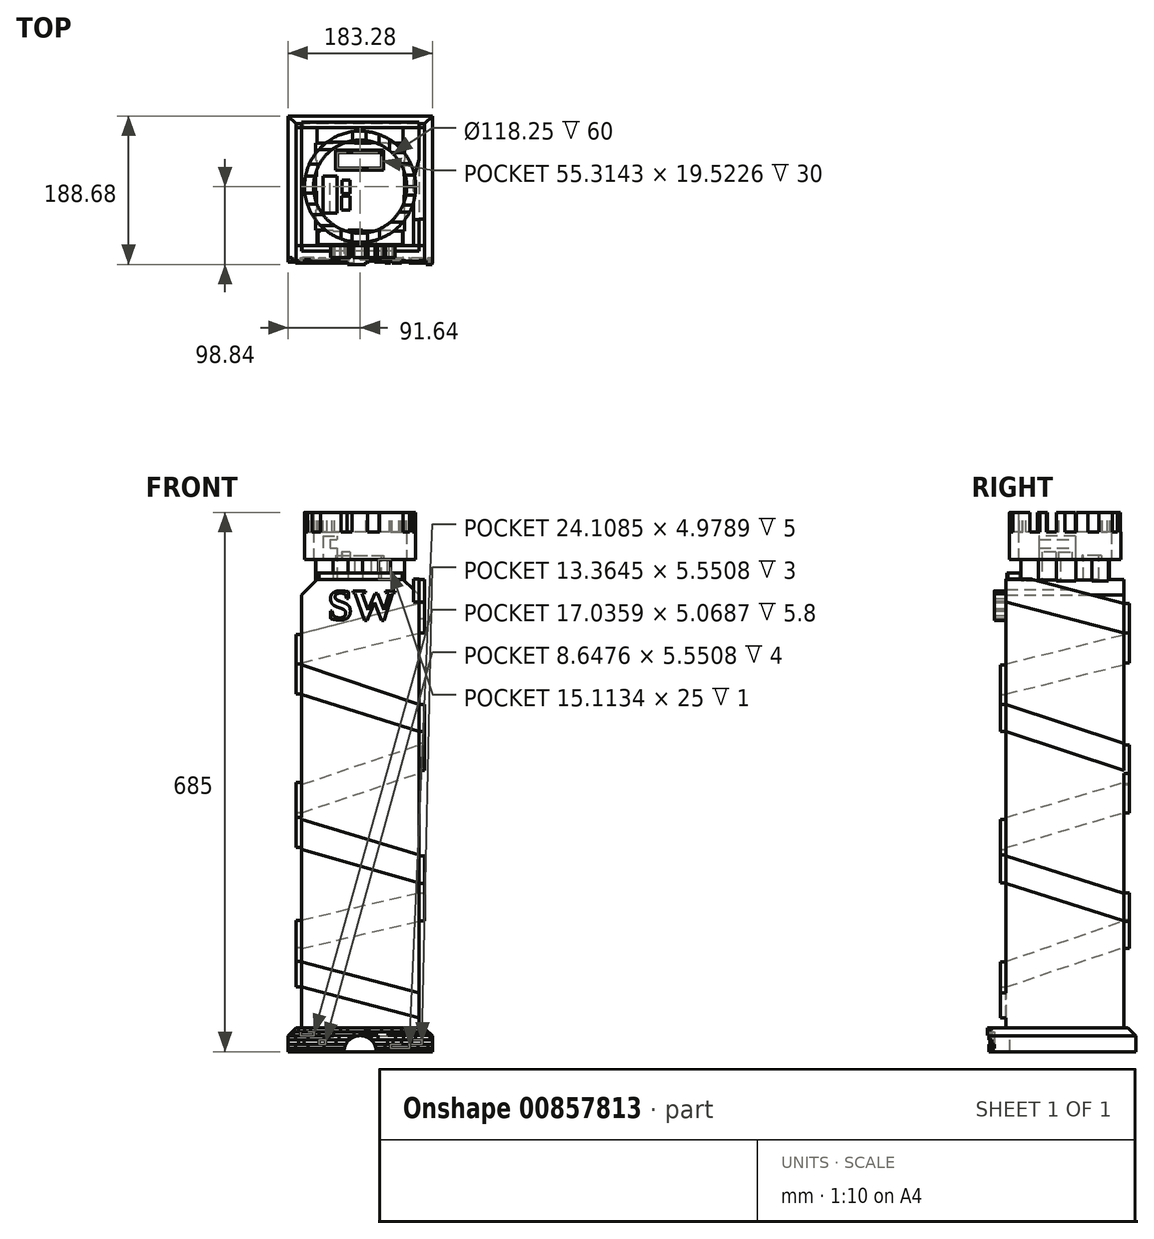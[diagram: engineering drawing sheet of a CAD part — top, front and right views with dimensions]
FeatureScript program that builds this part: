
annotation { "Feature Type Name" : "Feature", "Feature Type Description" : "" }
export const myFeature = defineFeature(function(context is Context, id is Id, definition is map)
    precondition{}
    {
        {
            var Q0;
            Q0=qCreatedBy(makeId("Top.planeOp"),FACE);
            var sketch = newSketch(context, id + "F0", { "sketchPlane" : qUnion([Q0])});
            skLineSegment(sketch, "E0.bottom", {"start": v(-74.68, 74.88) * mm, "end": v(74.68, 74.88) * mm});
            skLineSegment(sketch, "E0.top", {"start": v(-74.68, -74.88) * mm, "end": v(74.68, -74.88) * mm});
            skLineSegment(sketch, "E0.left", {"start": v(-74.68, 74.88) * mm, "end": v(-74.68, -74.88) * mm});
            skLineSegment(sketch, "E0.right", {"start": v(74.68, 74.88) * mm, "end": v(74.68, -74.88) * mm});
            skPoint(sketch, "E0.middle", {"position": v(0, 0) * mm});
            skSolve(sketch);
        }
        {
            var Q0;
            Q0=makeQuery(id+"F0.imprint","IMPRINT",FACE,{"disambiguationData":[TD([[makeQuery(id+"F0.imprint","IMPRINT",EDGE,{"derivedFrom":sQuery(id+"F0.wireOp",EDGE,"E0.bottom")}),-1.0]])]});
            extrude(context, id + "F1", {"entities" : qUnion([Q0]), "depth" : 600 * mm, "offsetDistance" : 25 * mm});
        }
        {
            var Q0;
            Q0=makeQuery(id+"F1.opExtrude","CAP_FACE",FACE,{"disambiguationData":[OSD([sQuery(id+"F0.wireOp",EDGE,"E0.bottom"),sQuery(id+"F0.wireOp",EDGE,"E0.top"),sQuery(id+"F0.wireOp",EDGE,"E0.left"),sQuery(id+"F0.wireOp",EDGE,"E0.right")])],"isStart":true});
            var sketch = newSketch(context, id + "F2", { "sketchPlane" : qUnion([Q0])});
            skLineSegment(sketch, "E1.bottom", {"start": v(-91.64, 89.84) * mm, "end": v(91.64, 89.84) * mm});
            skLineSegment(sketch, "E1.top", {"start": v(-91.64, -89.84) * mm, "end": v(91.64, -89.84) * mm});
            skLineSegment(sketch, "E1.left", {"start": v(-91.64, 89.84) * mm, "end": v(-91.64, -89.84) * mm});
            skLineSegment(sketch, "E1.right", {"start": v(91.64, 89.84) * mm, "end": v(91.64, -89.84) * mm});
            skPoint(sketch, "E1.middle", {"position": v(0, 0) * mm});
            skSolve(sketch);
        }
        {
            var Q0;
            Q0=makeQuery(id+"F1.opExtrude","CAP_FACE",FACE,{"disambiguationData":[OSD([sQuery(id+"F0.wireOp",EDGE,"E0.bottom"),sQuery(id+"F0.wireOp",EDGE,"E0.top"),sQuery(id+"F0.wireOp",EDGE,"E0.left"),sQuery(id+"F0.wireOp",EDGE,"E0.right")])],"isStart":false});
            var sketch = newSketch(context, id + "F3", { "sketchPlane" : qUnion([Q0])});
            skLineSegment(sketch, "E2.bottom", {"start": v(-54.57, 54.23) * mm, "end": v(54.57, 54.23) * mm});
            skLineSegment(sketch, "E2.top", {"start": v(-54.57, -54.23) * mm, "end": v(54.57, -54.23) * mm});
            skLineSegment(sketch, "E2.left", {"start": v(-54.57, 54.23) * mm, "end": v(-54.57, -54.23) * mm});
            skLineSegment(sketch, "E2.right", {"start": v(54.57, 54.23) * mm, "end": v(54.57, -54.23) * mm});
            skPoint(sketch, "E2.middle", {"position": v(0, 0) * mm});
            skSolve(sketch);
        }
        {
            var Q0;
            Q0=makeQuery(id+"F3.imprint","IMPRINT",FACE,{"disambiguationData":[TD([[makeQuery(id+"F3.imprint","IMPRINT",EDGE,{"derivedFrom":sQuery(id+"F3.wireOp",EDGE,"E2.bottom")}),-1.0]])]});
            extrude(context, id + "F4", {"entities" : qUnion([Q0]), "operationType" : NewBodyOperationType.ADD, "depth" : 25 * mm, "offsetDistance" : 25 * mm});
        }
        {
            var Q0;
            Q0=makeQuery(id+"F4.opExtrude","CAP_FACE",FACE,{"disambiguationData":[OSD([sQuery(id+"F3.wireOp",EDGE,"E2.bottom"),sQuery(id+"F3.wireOp",EDGE,"E2.top"),sQuery(id+"F3.wireOp",EDGE,"E2.left"),sQuery(id+"F3.wireOp",EDGE,"E2.right")])],"isStart":false});
            var sketch = newSketch(context, id + "F5", { "sketchPlane" : qUnion([Q0])});
            skCircle(sketch, "E3", {"center": v(0, 0) * mm, "radius": 70.63 * mm});
            skCircle(sketch, "E4", {"center": v(0, 0) * mm, "radius": 59.12 * mm});
            skSolve(sketch);
        }
        {
            var Q0;
            {var subQ0=sQuery(id+"F5.wireOp",EDGE,"E3");var subQ1=makeQuery(id+"F4.opExtrude","CAP_EDGE",EDGE,{"disambiguationData":[OSD([sQuery(id+"F3.wireOp",EDGE,"E2.bottom")])],"isStart":false});var subQ2=makeQuery(id+"F5.imprint","INTERSECT",VERTEX,{"disambiguationData":[OD(0.0)],"derivedFrom":[subQ1,subQ0]});Q0=makeQuery(id+"F5.imprint","IMPRINT",FACE,{"disambiguationData":[TD([[makeQuery(id+"F5.imprint","IMPRINT",EDGE,{"disambiguationData":[TD([[subQ2,-1.0]])],"derivedFrom":subQ0}),1.0]])]});}
            var Q1;
            {var subQ0=sQuery(id+"F5.wireOp",EDGE,"E3");var subQ1=makeQuery(id+"F4.opExtrude","CAP_EDGE",EDGE,{"disambiguationData":[OSD([sQuery(id+"F3.wireOp",EDGE,"E2.bottom")])],"isStart":false});var subQ2=makeQuery(id+"F5.imprint","INTERSECT",VERTEX,{"disambiguationData":[OD(1.0)],"derivedFrom":[subQ1,subQ0]});Q1=makeQuery(id+"F5.imprint","IMPRINT",FACE,{"disambiguationData":[TD([[makeQuery(id+"F5.imprint","IMPRINT",EDGE,{"disambiguationData":[TD([[subQ2,-1.0]])],"derivedFrom":subQ0}),1.0]])]});}
            var Q2;
            {var subQ0=sQuery(id+"F5.wireOp",EDGE,"E3");var subQ1=makeQuery(id+"F4.opExtrude","CAP_EDGE",EDGE,{"disambiguationData":[OSD([sQuery(id+"F3.wireOp",EDGE,"E2.left")])],"isStart":false});var subQ2=makeQuery(id+"F5.imprint","INTERSECT",VERTEX,{"disambiguationData":[OD(0.0)],"derivedFrom":[subQ1,subQ0]});Q2=makeQuery(id+"F5.imprint","IMPRINT",FACE,{"disambiguationData":[TD([[makeQuery(id+"F5.imprint","IMPRINT",EDGE,{"disambiguationData":[TD([[subQ2,-1.0]])],"derivedFrom":subQ0}),1.0]])]});}
            var Q3;
            {var subQ0=sQuery(id+"F5.wireOp",EDGE,"E3");var subQ1=makeQuery(id+"F4.opExtrude","CAP_EDGE",EDGE,{"disambiguationData":[OSD([sQuery(id+"F3.wireOp",EDGE,"E2.top")])],"isStart":false});var subQ2=makeQuery(id+"F5.imprint","INTERSECT",VERTEX,{"disambiguationData":[OD(0.0)],"derivedFrom":[subQ1,subQ0]});Q3=makeQuery(id+"F5.imprint","IMPRINT",FACE,{"disambiguationData":[TD([[makeQuery(id+"F5.imprint","IMPRINT",EDGE,{"disambiguationData":[TD([[subQ2,-1.0]])],"derivedFrom":subQ0}),1.0]])]});}
            var Q4;
            {var subQ0=sQuery(id+"F5.wireOp",EDGE,"E3");var subQ1=makeQuery(id+"F4.opExtrude","CAP_EDGE",EDGE,{"disambiguationData":[OSD([sQuery(id+"F3.wireOp",EDGE,"E2.left")])],"isStart":false});var subQ2=makeQuery(id+"F5.imprint","INTERSECT",VERTEX,{"disambiguationData":[OD(1.0)],"derivedFrom":[subQ1,subQ0]});Q4=makeQuery(id+"F5.imprint","IMPRINT",FACE,{"disambiguationData":[TD([[makeQuery(id+"F5.imprint","IMPRINT",EDGE,{"disambiguationData":[TD([[subQ2,-1.0]])],"derivedFrom":subQ0}),1.0]])]});}
            var Q5;
            {var subQ0=sQuery(id+"F5.wireOp",EDGE,"E3");var subQ1=makeQuery(id+"F4.opExtrude","CAP_EDGE",EDGE,{"disambiguationData":[OSD([sQuery(id+"F3.wireOp",EDGE,"E2.top")])],"isStart":false});var subQ2=makeQuery(id+"F5.imprint","INTERSECT",VERTEX,{"disambiguationData":[OD(1.0)],"derivedFrom":[subQ1,subQ0]});Q5=makeQuery(id+"F5.imprint","IMPRINT",FACE,{"disambiguationData":[TD([[makeQuery(id+"F5.imprint","IMPRINT",EDGE,{"disambiguationData":[TD([[subQ2,-1.0]])],"derivedFrom":subQ0}),1.0]])]});}
            var Q6;
            {var subQ0=sQuery(id+"F5.wireOp",EDGE,"E3");var subQ1=makeQuery(id+"F4.opExtrude","CAP_EDGE",EDGE,{"disambiguationData":[OSD([sQuery(id+"F3.wireOp",EDGE,"E2.right")])],"isStart":false});var subQ2=makeQuery(id+"F5.imprint","INTERSECT",VERTEX,{"disambiguationData":[OD(0.0)],"derivedFrom":[subQ1,subQ0]});Q6=makeQuery(id+"F5.imprint","IMPRINT",FACE,{"disambiguationData":[TD([[makeQuery(id+"F5.imprint","IMPRINT",EDGE,{"disambiguationData":[TD([[subQ2,1.0]])],"derivedFrom":subQ0}),1.0]])]});}
            var Q7;
            {var subQ0=sQuery(id+"F5.wireOp",EDGE,"E3");var subQ1=makeQuery(id+"F4.opExtrude","CAP_EDGE",EDGE,{"disambiguationData":[OSD([sQuery(id+"F3.wireOp",EDGE,"E2.bottom")])],"isStart":false});var subQ2=makeQuery(id+"F5.imprint","INTERSECT",VERTEX,{"disambiguationData":[OD(0.0)],"derivedFrom":[subQ1,subQ0]});Q7=makeQuery(id+"F5.imprint","IMPRINT",FACE,{"disambiguationData":[TD([[makeQuery(id+"F5.imprint","IMPRINT",EDGE,{"disambiguationData":[TD([[subQ2,1.0]])],"derivedFrom":subQ0}),1.0]])]});}
            extrude(context, id + "F6", {"entities" : qUnion([Q0, Q1, Q2, Q3, Q4, Q5, Q6, Q7]), "operationType" : NewBodyOperationType.ADD, "depth" : 60 * mm, "offsetDistance" : 25 * mm});
        }
        {
            var Q0;
            Q0=makeQuery(id+"F6.opExtrude","CAP_FACE",FACE,{"disambiguationData":[OSD([sQuery(id+"F5.wireOp",EDGE,"E3"),sQuery(id+"F5.wireOp",EDGE,"E4")])],"isStart":false});
            var sketch = newSketch(context, id + "F7", { "sketchPlane" : qUnion([Q0])});
            skLineSegment(sketch, "E5.bottom", {"start": v(-9.47, 76.95) * mm, "end": v(7.75, 76.95) * mm});
            skLineSegment(sketch, "E5.top", {"start": v(-9.47, 53.88) * mm, "end": v(7.75, 53.88) * mm});
            skLineSegment(sketch, "E5.left", {"start": v(-9.47, 76.95) * mm, "end": v(-9.47, 53.88) * mm});
            skLineSegment(sketch, "E5.right", {"start": v(7.75, 76.95) * mm, "end": v(7.75, 53.88) * mm});
            skLineSegment(sketch, "E6.bottom", {"start": v(37.36, 69.37) * mm, "end": v(24.27, 69.37) * mm});
            skLineSegment(sketch, "E6.top", {"start": v(37.36, 43.2) * mm, "end": v(24.27, 43.2) * mm});
            skLineSegment(sketch, "E6.left", {"start": v(37.36, 69.37) * mm, "end": v(37.36, 43.2) * mm});
            skLineSegment(sketch, "E6.right", {"start": v(24.27, 69.37) * mm, "end": v(24.27, 43.2) * mm});
            skPoint(sketch, "E7.firstSnap0", {"position": v(30.81, 43.2) * mm});
            skLineSegment(sketch, "E7.bottom", {"start": v(65.59, 43.2) * mm, "end": v(39.77, 43.2) * mm});
            skLineSegment(sketch, "E7.top", {"start": v(65.59, 29.1) * mm, "end": v(39.77, 29.1) * mm});
            skLineSegment(sketch, "E7.left", {"start": v(65.59, 43.2) * mm, "end": v(65.59, 29.1) * mm});
            skLineSegment(sketch, "E7.right", {"start": v(39.77, 43.2) * mm, "end": v(39.77, 29.1) * mm});
            skLineSegment(sketch, "E8.bottom", {"start": v(74.54, 14.63) * mm, "end": v(52.5, 14.63) * mm});
            skLineSegment(sketch, "E8.top", {"start": v(74.54, 0) * mm, "end": v(52.5, 0) * mm});
            skLineSegment(sketch, "E8.left", {"start": v(74.54, 14.63) * mm, "end": v(74.54, 0) * mm});
            skLineSegment(sketch, "E8.right", {"start": v(52.5, 14.63) * mm, "end": v(52.5, 0) * mm});
            skLineSegment(sketch, "E9.bottom", {"start": v(71.44, -23.58) * mm, "end": v(42.86, -23.58) * mm});
            skLineSegment(sketch, "E9.top", {"start": v(71.44, -10.85) * mm, "end": v(42.86, -10.85) * mm});
            skLineSegment(sketch, "E9.left", {"start": v(71.44, -23.58) * mm, "end": v(71.44, -10.85) * mm});
            skLineSegment(sketch, "E9.right", {"start": v(42.86, -23.58) * mm, "end": v(42.86, -10.85) * mm});
            skLineSegment(sketch, "E10.bottom", {"start": v(29.78, -32.2) * mm, "end": v(69.03, -32.2) * mm});
            skLineSegment(sketch, "E10.top", {"start": v(29.78, -44.93) * mm, "end": v(69.03, -44.93) * mm});
            skLineSegment(sketch, "E10.left", {"start": v(29.78, -32.2) * mm, "end": v(29.78, -44.93) * mm});
            skLineSegment(sketch, "E10.right", {"start": v(69.03, -32.2) * mm, "end": v(69.03, -44.93) * mm});
            skLineSegment(sketch, "E11.bottom", {"start": v(9.47, -45.27) * mm, "end": v(24.96, -45.27) * mm});
            skLineSegment(sketch, "E11.top", {"start": v(9.47, -75.23) * mm, "end": v(24.96, -75.23) * mm});
            skLineSegment(sketch, "E11.left", {"start": v(9.47, -45.27) * mm, "end": v(9.47, -75.23) * mm});
            skLineSegment(sketch, "E11.right", {"start": v(24.96, -45.27) * mm, "end": v(24.96, -75.23) * mm});
            skLineSegment(sketch, "E12.bottom", {"start": v(-24.27, -41.14) * mm, "end": v(-10.5, -41.14) * mm});
            skLineSegment(sketch, "E12.top", {"start": v(-24.27, -74.88) * mm, "end": v(-10.5, -74.88) * mm});
            skLineSegment(sketch, "E12.left", {"start": v(-24.27, -41.14) * mm, "end": v(-24.27, -74.88) * mm});
            skLineSegment(sketch, "E12.right", {"start": v(-10.5, -41.14) * mm, "end": v(-10.5, -74.88) * mm});
            skLineSegment(sketch, "E13.bottom", {"start": v(-71.78, -35.29) * mm, "end": v(-32.25, -35.29) * mm});
            skLineSegment(sketch, "E13.top", {"start": v(-71.78, -49.55) * mm, "end": v(-32.25, -49.55) * mm});
            skLineSegment(sketch, "E13.left", {"start": v(-71.78, -35.29) * mm, "end": v(-71.78, -49.55) * mm});
            skLineSegment(sketch, "E13.right", {"start": v(-32.25, -35.29) * mm, "end": v(-32.25, -49.55) * mm});
            skLineSegment(sketch, "E14.bottom", {"start": v(-75.23, -8.1) * mm, "end": v(-46.65, -8.1) * mm});
            skLineSegment(sketch, "E14.top", {"start": v(-75.23, -22.2) * mm, "end": v(-46.65, -22.2) * mm});
            skLineSegment(sketch, "E14.left", {"start": v(-75.23, -8.1) * mm, "end": v(-75.23, -22.2) * mm});
            skLineSegment(sketch, "E14.right", {"start": v(-46.65, -8.1) * mm, "end": v(-46.65, -22.2) * mm});
            skLineSegment(sketch, "E15.bottom", {"start": v(-73.5, 28.4) * mm, "end": v(-47.68, 28.4) * mm});
            skLineSegment(sketch, "E15.top", {"start": v(-73.5, 13.26) * mm, "end": v(-47.68, 13.26) * mm});
            skLineSegment(sketch, "E15.left", {"start": v(-73.5, 28.4) * mm, "end": v(-73.5, 13.26) * mm});
            skLineSegment(sketch, "E15.right", {"start": v(-47.68, 28.4) * mm, "end": v(-47.68, 13.26) * mm});
            skLineSegment(sketch, "E16.bottom", {"start": v(-67.3, 47.34) * mm, "end": v(-16.29, 47.34) * mm});
            skLineSegment(sketch, "E16.top", {"start": v(-67.3, 56.84) * mm, "end": v(-16.29, 56.84) * mm});
            skLineSegment(sketch, "E16.left", {"start": v(-67.3, 47.34) * mm, "end": v(-67.3, 56.84) * mm});
            skLineSegment(sketch, "E16.right", {"start": v(-16.29, 47.34) * mm, "end": v(-16.29, 56.84) * mm});
            skSolve(sketch);
        }
        {
            var Q0;
            {var subQ0=sQuery(id+"F7.wireOp",EDGE,"E6.left");var subQ1=makeQuery(id+"F6.opExtrude","CAP_EDGE",EDGE,{"disambiguationData":[OSD([sQuery(id+"F5.wireOp",EDGE,"E3")])],"isStart":false});var subQ2=makeQuery(id+"F7.imprint","INTERSECT",VERTEX,{"derivedFrom":[subQ1,subQ0]});Q0=makeQuery(id+"F7.imprint","IMPRINT",FACE,{"disambiguationData":[TD([[makeQuery(id+"F7.imprint","IMPRINT",EDGE,{"disambiguationData":[TD([[subQ2,-1.0]])],"derivedFrom":subQ0}),-1.0]])]});}
            var Q1;
            {var subQ0=sQuery(id+"F7.wireOp",EDGE,"E5.left");var subQ1=makeQuery(id+"F6.opExtrude","CAP_EDGE",EDGE,{"disambiguationData":[OSD([sQuery(id+"F5.wireOp",EDGE,"E3")])],"isStart":false});var subQ2=makeQuery(id+"F7.imprint","INTERSECT",VERTEX,{"derivedFrom":[subQ1,subQ0]});Q1=makeQuery(id+"F7.imprint","IMPRINT",FACE,{"disambiguationData":[TD([[makeQuery(id+"F7.imprint","IMPRINT",EDGE,{"disambiguationData":[TD([[subQ2,-1.0]])],"derivedFrom":subQ0}),1.0]])]});}
            var Q2;
            {var subQ0=sQuery(id+"F7.wireOp",EDGE,"E16.bottom");var subQ1=makeQuery(id+"F6.opExtrude","CAP_EDGE",EDGE,{"disambiguationData":[OSD([sQuery(id+"F5.wireOp",EDGE,"E3")])],"isStart":false});var subQ2=makeQuery(id+"F7.imprint","INTERSECT",VERTEX,{"derivedFrom":[subQ1,subQ0]});Q2=makeQuery(id+"F7.imprint","IMPRINT",FACE,{"disambiguationData":[TD([[makeQuery(id+"F7.imprint","IMPRINT",EDGE,{"disambiguationData":[TD([[subQ2,-1.0]])],"derivedFrom":subQ0}),1.0]])]});}
            var Q3;
            {var subQ0=sQuery(id+"F7.wireOp",EDGE,"E15.bottom");var subQ1=makeQuery(id+"F6.opExtrude","CAP_EDGE",EDGE,{"disambiguationData":[OSD([sQuery(id+"F5.wireOp",EDGE,"E3")])],"isStart":false});var subQ2=makeQuery(id+"F7.imprint","INTERSECT",VERTEX,{"derivedFrom":[subQ1,subQ0]});Q3=makeQuery(id+"F7.imprint","IMPRINT",FACE,{"disambiguationData":[TD([[makeQuery(id+"F7.imprint","IMPRINT",EDGE,{"disambiguationData":[TD([[subQ2,-1.0]])],"derivedFrom":subQ0}),-1.0]])]});}
            var Q4;
            {var subQ0=sQuery(id+"F7.wireOp",EDGE,"E14.bottom");var subQ1=makeQuery(id+"F6.opExtrude","CAP_EDGE",EDGE,{"disambiguationData":[OSD([sQuery(id+"F5.wireOp",EDGE,"E3")])],"isStart":false});var subQ2=makeQuery(id+"F7.imprint","INTERSECT",VERTEX,{"derivedFrom":[subQ1,subQ0]});Q4=makeQuery(id+"F7.imprint","IMPRINT",FACE,{"disambiguationData":[TD([[makeQuery(id+"F7.imprint","IMPRINT",EDGE,{"disambiguationData":[TD([[subQ2,-1.0]])],"derivedFrom":subQ0}),-1.0]])]});}
            var Q5;
            {var subQ0=sQuery(id+"F7.wireOp",EDGE,"E13.bottom");var subQ1=makeQuery(id+"F6.opExtrude","CAP_EDGE",EDGE,{"disambiguationData":[OSD([sQuery(id+"F5.wireOp",EDGE,"E3")])],"isStart":false});var subQ2=makeQuery(id+"F7.imprint","INTERSECT",VERTEX,{"derivedFrom":[subQ1,subQ0]});Q5=makeQuery(id+"F7.imprint","IMPRINT",FACE,{"disambiguationData":[TD([[makeQuery(id+"F7.imprint","IMPRINT",EDGE,{"disambiguationData":[TD([[subQ2,-1.0]])],"derivedFrom":subQ0}),-1.0]])]});}
            var Q6;
            {var subQ0=sQuery(id+"F7.wireOp",EDGE,"E12.left");var subQ1=makeQuery(id+"F6.opExtrude","CAP_EDGE",EDGE,{"disambiguationData":[OSD([sQuery(id+"F5.wireOp",EDGE,"E3")])],"isStart":false});var subQ2=makeQuery(id+"F7.imprint","INTERSECT",VERTEX,{"derivedFrom":[subQ1,subQ0]});Q6=makeQuery(id+"F7.imprint","IMPRINT",FACE,{"disambiguationData":[TD([[makeQuery(id+"F7.imprint","IMPRINT",EDGE,{"disambiguationData":[TD([[subQ2,1.0]])],"derivedFrom":subQ0}),1.0]])]});}
            var Q7;
            {var subQ0=sQuery(id+"F7.wireOp",EDGE,"E11.left");var subQ1=makeQuery(id+"F6.opExtrude","CAP_EDGE",EDGE,{"disambiguationData":[OSD([sQuery(id+"F5.wireOp",EDGE,"E3")])],"isStart":false});var subQ2=makeQuery(id+"F7.imprint","INTERSECT",VERTEX,{"derivedFrom":[subQ1,subQ0]});Q7=makeQuery(id+"F7.imprint","IMPRINT",FACE,{"disambiguationData":[TD([[makeQuery(id+"F7.imprint","IMPRINT",EDGE,{"disambiguationData":[TD([[subQ2,1.0]])],"derivedFrom":subQ0}),1.0]])]});}
            var Q8;
            {var subQ0=sQuery(id+"F7.wireOp",EDGE,"E10.bottom");var subQ1=makeQuery(id+"F6.opExtrude","CAP_EDGE",EDGE,{"disambiguationData":[OSD([sQuery(id+"F5.wireOp",EDGE,"E3")])],"isStart":false});var subQ2=makeQuery(id+"F7.imprint","INTERSECT",VERTEX,{"derivedFrom":[subQ1,subQ0]});Q8=makeQuery(id+"F7.imprint","IMPRINT",FACE,{"disambiguationData":[TD([[makeQuery(id+"F7.imprint","IMPRINT",EDGE,{"disambiguationData":[TD([[subQ2,1.0]])],"derivedFrom":subQ0}),-1.0]])]});}
            var Q9;
            {var subQ0=sQuery(id+"F7.wireOp",EDGE,"E9.bottom");var subQ1=makeQuery(id+"F6.opExtrude","CAP_EDGE",EDGE,{"disambiguationData":[OSD([sQuery(id+"F5.wireOp",EDGE,"E3")])],"isStart":false});var subQ2=makeQuery(id+"F7.imprint","INTERSECT",VERTEX,{"derivedFrom":[subQ1,subQ0]});Q9=makeQuery(id+"F7.imprint","IMPRINT",FACE,{"disambiguationData":[TD([[makeQuery(id+"F7.imprint","IMPRINT",EDGE,{"disambiguationData":[TD([[subQ2,-1.0]])],"derivedFrom":subQ0}),-1.0]])]});}
            var Q10;
            {var subQ0=sQuery(id+"F7.wireOp",EDGE,"E8.bottom");var subQ1=makeQuery(id+"F6.opExtrude","CAP_EDGE",EDGE,{"disambiguationData":[OSD([sQuery(id+"F5.wireOp",EDGE,"E3")])],"isStart":false});var subQ2=makeQuery(id+"F7.imprint","INTERSECT",VERTEX,{"derivedFrom":[subQ1,subQ0]});Q10=makeQuery(id+"F7.imprint","IMPRINT",FACE,{"disambiguationData":[TD([[makeQuery(id+"F7.imprint","IMPRINT",EDGE,{"disambiguationData":[TD([[subQ2,-1.0]])],"derivedFrom":subQ0}),1.0]])]});}
            var Q11;
            {var subQ0=sQuery(id+"F7.wireOp",EDGE,"E7.bottom");var subQ1=makeQuery(id+"F6.opExtrude","CAP_EDGE",EDGE,{"disambiguationData":[OSD([sQuery(id+"F5.wireOp",EDGE,"E3")])],"isStart":false});var subQ2=makeQuery(id+"F7.imprint","INTERSECT",VERTEX,{"derivedFrom":[subQ1,subQ0]});Q11=makeQuery(id+"F7.imprint","IMPRINT",FACE,{"disambiguationData":[TD([[makeQuery(id+"F7.imprint","IMPRINT",EDGE,{"disambiguationData":[TD([[subQ2,-1.0]])],"derivedFrom":subQ0}),1.0]])]});}
            extrude(context, id + "F8", {"entities" : qUnion([Q0, Q1, Q2, Q3, Q4, Q5, Q6, Q7, Q8, Q9, Q10, Q11]), "operationType" : NewBodyOperationType.REMOVE, "oppositeDirection" : true, "depth" : 25 * mm, "offsetDistance" : 25 * mm});
        }
        {
            var Q0;
            Q0=makeQuery(id+"F2.imprint","IMPRINT",FACE,{"disambiguationData":[TD([[makeQuery(id+"F2.imprint","IMPRINT",EDGE,{"derivedFrom":sQuery(id+"F2.wireOp",EDGE,"E1.bottom")}),-1.0]])]});
            extrude(context, id + "F9", {"entities" : qUnion([Q0]), "operationType" : NewBodyOperationType.ADD, "oppositeDirection" : true, "depth" : 30 * mm, "offsetDistance" : 25 * mm});
        }
        {
            var Q0;
            Q0=makeQuery(id+"F1.opExtrude","SWEPT_FACE",FACE,{"disambiguationData":[OSD([sQuery(id+"F0.wireOp",EDGE,"E0.top")])]});
            var sketch = newSketch(context, id + "F10", { "sketchPlane" : qUnion([Q0])});
            skLineSegment(sketch, "E17", {"start": v(74.68, 42.98) * mm, "end": v(-74.68, 82.43) * mm});
            skLineSegment(sketch, "E18", {"start": v(74.68, 74.92) * mm, "end": v(-74.68, 114.36) * mm});
            skSolve(sketch);
        }
        {
            var Q0;
            Q0=makeQuery(id+"F1.opExtrude","SWEPT_FACE",FACE,{"disambiguationData":[OSD([sQuery(id+"F0.wireOp",EDGE,"E0.left")])]});
            var sketch = newSketch(context, id + "F11", { "sketchPlane" : qUnion([Q0])});
            skLineSegment(sketch, "E19", {"start": v(74.88, 114.53) * mm, "end": v(-74.88, 166.66) * mm});
            skLineSegment(sketch, "E20", {"start": v(74.88, 82.26) * mm, "end": v(-74.88, 132.53) * mm});
            skSolve(sketch);
        }
        {
            var Q0;
            Q0=makeQuery(id+"F1.opExtrude","SWEPT_FACE",FACE,{"disambiguationData":[OSD([sQuery(id+"F0.wireOp",EDGE,"E0.bottom")])]});
            var sketch = newSketch(context, id + "F12", { "sketchPlane" : qUnion([Q0])});
            skLineSegment(sketch, "E21", {"start": v(74.68, 167.39) * mm, "end": v(-74.68, 201.82) * mm});
            skLineSegment(sketch, "E22", {"start": v(74.68, 131.22) * mm, "end": v(-74.68, 165.65) * mm});
            skSolve(sketch);
        }
        {
            var Q0;
            Q0=makeQuery(id+"F1.opExtrude","SWEPT_FACE",FACE,{"disambiguationData":[OSD([sQuery(id+"F0.wireOp",EDGE,"E0.right")])]});
            var sketch = newSketch(context, id + "F13", { "sketchPlane" : qUnion([Q0])});
            skLineSegment(sketch, "E23", {"start": v(74.88, 200.88) * mm, "end": v(-74.88, 248.94) * mm});
            skLineSegment(sketch, "E24", {"start": v(74.88, 165.93) * mm, "end": v(-74.88, 213.99) * mm});
            skSolve(sketch);
        }
        {
            var Q0;
            {var subQ0=sQuery(id+"F10.wireOp",EDGE,"E18");Q0=makeQuery(id+"F10.imprint","IMPRINT",FACE,{"disambiguationData":[TD([[makeQuery(id+"F10.imprint","IMPRINT",EDGE,{"derivedFrom":subQ0}),-1.0]])]});}
            var sketch = newSketch(context, id + "F14", { "sketchPlane" : qUnion([Q0])});
            skLineSegment(sketch, "E25", {"start": v(74.9, 249.82) * mm, "end": v(-76.45, 295.53) * mm});
            skLineSegment(sketch, "E26", {"start": v(76.45, 213.99) * mm, "end": v(-76.45, 257.67) * mm});
            skSolve(sketch);
        }
        {
            var Q0;
            {var subQ0=sQuery(id+"F11.wireOp",EDGE,"E19");Q0=makeQuery(id+"F11.imprint","IMPRINT",FACE,{"disambiguationData":[TD([[makeQuery(id+"F11.imprint","IMPRINT",EDGE,{"derivedFrom":subQ0}),-1.0]])]});}
            var sketch = newSketch(context, id + "F15", { "sketchPlane" : qUnion([Q0])});
            skLineSegment(sketch, "E27", {"start": v(76.45, 297) * mm, "end": v(-75, 342.13) * mm});
            skLineSegment(sketch, "E28", {"start": v(75, 259.13) * mm, "end": v(-75, 303.84) * mm});
            skSolve(sketch);
        }
        {
            var Q0;
            {var subQ0=sQuery(id+"F12.wireOp",EDGE,"E21");Q0=makeQuery(id+"F12.imprint","IMPRINT",FACE,{"disambiguationData":[TD([[makeQuery(id+"F12.imprint","IMPRINT",EDGE,{"derivedFrom":subQ0}),-1.0]])]});}
            var sketch = newSketch(context, id + "F16", { "sketchPlane" : qUnion([Q0])});
            skLineSegment(sketch, "E29", {"start": v(72.56, 340.05) * mm, "end": v(-76.45, 390.19) * mm});
            skLineSegment(sketch, "E30", {"start": v(76.45, 302.82) * mm, "end": v(-76.45, 354.26) * mm});
            skLineSegment(sketch, "E31", {"start": v(72.56, 340.05) * mm, "end": v(74.65, 339.46) * mm});
            skLineSegment(sketch, "E32", {"start": v(-76.45, 390.19) * mm, "end": v(-76.45, 354.26) * mm});
            skLineSegment(sketch, "E33", {"start": v(74.65, 339.46) * mm, "end": v(76.45, 302.82) * mm});
            skSolve(sketch);
        }
        {
            var Q0;
            {var subQ0=sQuery(id+"F13.wireOp",EDGE,"E23");Q0=makeQuery(id+"F13.imprint","IMPRINT",FACE,{"disambiguationData":[TD([[makeQuery(id+"F13.imprint","IMPRINT",EDGE,{"derivedFrom":subQ0}),-1.0]])]});}
            var sketch = newSketch(context, id + "F17", { "sketchPlane" : qUnion([Q0])});
            skLineSegment(sketch, "E34", {"start": v(75, 391.64) * mm, "end": v(-75, 441.16) * mm});
            skLineSegment(sketch, "E35", {"start": v(76.45, 356.7) * mm, "end": v(-75, 406.69) * mm});
            skSolve(sketch);
        }
        {
            var Q0;
            {var subQ0=sQuery(id+"F10.wireOp",EDGE,"E18");Q0=makeQuery(id+"F10.imprint","IMPRINT",FACE,{"disambiguationData":[TD([[makeQuery(id+"F10.imprint","IMPRINT",EDGE,{"derivedFrom":subQ0}),-1.0]])]});}
            var sketch = newSketch(context, id + "F18", { "sketchPlane" : qUnion([Q0])});
            skLineSegment(sketch, "E36", {"start": v(75.9, 440.45) * mm, "end": v(-73.68, 491.16) * mm});
            skLineSegment(sketch, "E37", {"start": v(74.17, 406.95) * mm, "end": v(-73.68, 453.3) * mm});
            skLineSegment(sketch, "E38", {"start": v(74.17, 406.95) * mm, "end": v(74.72, 406.78) * mm});
            skLineSegment(sketch, "E39", {"start": v(-73.68, 453.3) * mm, "end": v(-74.71, 453.62) * mm});
            skLineSegment(sketch, "E40", {"start": v(-73.68, 491.16) * mm, "end": v(-74.71, 491.48) * mm});
            skSolve(sketch);
        }
        {
            var Q0;
            {var subQ1=sQuery(id+"F0.wireOp",EDGE,"E0.left");var subQ3=makeQuery(id+"F1.opExtrude","CAP_EDGE",EDGE,{"disambiguationData":[OSD([subQ1])],"isStart":false});var subQ10=makeQuery(id+"F11.imprint","IMPRINT",EDGE,{"derivedFrom":subQ3});Q0=makeQuery(id+"F15.imprint","IMPRINT",FACE,{"disambiguationData":[TD([[makeQuery(id+"F15.imprint","IMPRINT",EDGE,{"derivedFrom":subQ10}),-1.0]])]});}
            var sketch = newSketch(context, id + "F19", { "sketchPlane" : qUnion([Q0])});
            skLineSegment(sketch, "E41", {"start": v(76.45, 492.12) * mm, "end": v(-75, 529.98) * mm});
            skLineSegment(sketch, "E42", {"start": v(75, 454.26) * mm, "end": v(-75, 491.76) * mm});
            skSolve(sketch);
        }
        {
            var Q0;
            {var subQ1=sQuery(id+"F0.wireOp",EDGE,"E0.bottom");var subQ3=makeQuery(id+"F1.opExtrude","CAP_EDGE",EDGE,{"disambiguationData":[OSD([subQ1])],"isStart":false});var subQ10=makeQuery(id+"F12.imprint","IMPRINT",EDGE,{"derivedFrom":subQ3});Q0=makeQuery(id+"F16.imprint","IMPRINT",FACE,{"disambiguationData":[TD([[makeQuery(id+"F16.imprint","IMPRINT",EDGE,{"derivedFrom":subQ10}),1.0]])]});}
            var sketch = newSketch(context, id + "F20", { "sketchPlane" : qUnion([Q0])});
            skLineSegment(sketch, "E43", {"start": v(73.54, 531.44) * mm, "end": v(-75, 569.3) * mm});
            skLineSegment(sketch, "E44", {"start": v(75, 493.58) * mm, "end": v(-75, 531.81) * mm});
            skLineSegment(sketch, "E45", {"start": v(73.54, 531.44) * mm, "end": v(74.7, 531.14) * mm});
            skSolve(sketch);
        }
        {
            var Q0;
            {var subQ1=sQuery(id+"F0.wireOp",EDGE,"E0.right");var subQ3=makeQuery(id+"F1.opExtrude","CAP_EDGE",EDGE,{"disambiguationData":[OSD([subQ1])],"isStart":false});var subQ10=makeQuery(id+"F13.imprint","IMPRINT",EDGE,{"derivedFrom":subQ3});Q0=makeQuery(id+"F17.imprint","IMPRINT",FACE,{"disambiguationData":[TD([[makeQuery(id+"F17.imprint","IMPRINT",EDGE,{"derivedFrom":subQ10}),1.0]])]});}
            var sketch = newSketch(context, id + "F21", { "sketchPlane" : qUnion([Q0])});
            skLineSegment(sketch, "E46", {"start": v(75.08, 569.22) * mm, "end": v(-42.03, 600.15) * mm});
            skLineSegment(sketch, "E47", {"start": v(74.7, 531.71) * mm, "end": v(-74.94, 571.23) * mm});
            skLineSegment(sketch, "E48", {"start": v(-74.94, 571.23) * mm, "end": v(-74.94, 600.15) * mm});
            skLineSegment(sketch, "E49", {"start": v(-74.94, 600.15) * mm, "end": v(-42.03, 600.15) * mm});
            skLineSegment(sketch, "E50", {"start": v(75.08, 569.22) * mm, "end": v(74.7, 531.71) * mm});
            skSolve(sketch);
        }
        {
            var Q0;
            {var subQ0=sQuery(id+"F11.wireOp",EDGE,"E19");Q0=makeQuery(id+"F11.imprint","IMPRINT",FACE,{"disambiguationData":[TD([[makeQuery(id+"F11.imprint","IMPRINT",EDGE,{"derivedFrom":subQ0}),1.0]])]});}
            var Q1;
            Q1 = qSketchRegion(id + "F21", true);
            extrude(context, id + "F22", {"entities" : qUnion([Q0, Q1]), "operationType" : NewBodyOperationType.ADD, "depth" : 7 * mm, "offsetDistance" : 25 * mm});
        }
        {
            var Q0;
            {var subQ0=sQuery(id+"F10.wireOp",EDGE,"E17");Q0=makeQuery(id+"F10.imprint","IMPRINT",FACE,{"disambiguationData":[TD([[makeQuery(id+"F10.imprint","IMPRINT",EDGE,{"derivedFrom":subQ0}),-1.0]])]});}
            extrude(context, id + "F23", {"entities" : qUnion([Q0]), "operationType" : NewBodyOperationType.ADD, "depth" : 7 * mm, "offsetDistance" : 25 * mm});
        }
        {
            var Q0;
            {var subQ0=sQuery(id+"F12.wireOp",EDGE,"E21");Q0=makeQuery(id+"F12.imprint","IMPRINT",FACE,{"disambiguationData":[TD([[makeQuery(id+"F12.imprint","IMPRINT",EDGE,{"derivedFrom":subQ0}),1.0]])]});}
            extrude(context, id + "F24", {"entities" : qUnion([Q0]), "operationType" : NewBodyOperationType.ADD, "depth" : 7 * mm, "offsetDistance" : 25 * mm});
        }
        {
            var Q0;
            {var subQ0=sQuery(id+"F13.wireOp",EDGE,"E23");Q0=makeQuery(id+"F13.imprint","IMPRINT",FACE,{"disambiguationData":[TD([[makeQuery(id+"F13.imprint","IMPRINT",EDGE,{"derivedFrom":subQ0}),1.0]])]});}
            extrude(context, id + "F25", {"entities" : qUnion([Q0]), "operationType" : NewBodyOperationType.ADD, "depth" : 7 * mm, "offsetDistance" : 25 * mm});
        }
        {
            var Q0;
            {var subQ0=sQuery(id+"F14.wireOp",EDGE,"E25");var subQ1=sQuery(id+"F0.wireOp",EDGE,"E0.top");var subQ2=makeQuery(id+"F1.opExtrude","SWEPT_EDGE",EDGE,{"disambiguationData":[OSD([subQ1,sQuery(id+"F0.wireOp",EDGE,"E0.left")])]});var subQ3=makeQuery(id+"F1.opExtrude","CAP_EDGE",EDGE,{"disambiguationData":[OSD([subQ1])],"isStart":false});var subQ5=makeQuery(id+"F10.imprint","IMPRINT",EDGE,{"disambiguationData":[TD([[makeQuery(id+"F10.imprint","INTERSECT",VERTEX,{"derivedFrom":[subQ3,subQ2]}),-1.0]])],"derivedFrom":subQ2});var subQ6=makeQuery(id+"F14.imprint","INTERSECT",VERTEX,{"derivedFrom":[subQ5,subQ0]});Q0=makeQuery(id+"F14.imprint","IMPRINT",FACE,{"disambiguationData":[TD([[makeQuery(id+"F14.imprint","IMPRINT",EDGE,{"disambiguationData":[TD([[subQ6,1.0]])],"derivedFrom":subQ0}),1.0]])]});}
            extrude(context, id + "F26", {"entities" : qUnion([Q0]), "operationType" : NewBodyOperationType.ADD, "depth" : 7 * mm, "offsetDistance" : 25 * mm});
        }
        {
            var Q0;
            {var subQ0=sQuery(id+"F15.wireOp",EDGE,"E27");var subQ1=sQuery(id+"F0.wireOp",EDGE,"E0.left");var subQ2=makeQuery(id+"F1.opExtrude","SWEPT_EDGE",EDGE,{"disambiguationData":[OSD([sQuery(id+"F0.wireOp",EDGE,"E0.bottom"),subQ1])]});var subQ3=makeQuery(id+"F1.opExtrude","CAP_EDGE",EDGE,{"disambiguationData":[OSD([subQ1])],"isStart":false});var subQ5=makeQuery(id+"F11.imprint","IMPRINT",EDGE,{"disambiguationData":[TD([[makeQuery(id+"F11.imprint","INTERSECT",VERTEX,{"derivedFrom":[subQ3,subQ2]}),-1.0]])],"derivedFrom":subQ2});var subQ6=makeQuery(id+"F15.imprint","INTERSECT",VERTEX,{"derivedFrom":[subQ5,subQ0]});Q0=makeQuery(id+"F15.imprint","IMPRINT",FACE,{"disambiguationData":[TD([[makeQuery(id+"F15.imprint","IMPRINT",EDGE,{"disambiguationData":[TD([[subQ6,1.0]])],"derivedFrom":subQ0}),1.0]])]});}
            extrude(context, id + "F27", {"entities" : qUnion([Q0]), "operationType" : NewBodyOperationType.ADD, "depth" : 7 * mm, "offsetDistance" : 25 * mm});
        }
        {
            var Q0;
            {var subQ1=sQuery(id+"F16.wireOp",EDGE,"E31");Q0=makeQuery(id+"F16.imprint","IMPRINT",FACE,{"disambiguationData":[TD([[makeQuery(id+"F16.imprint","IMPRINT",EDGE,{"derivedFrom":subQ1}),-1.0]])]});}
            extrude(context, id + "F28", {"entities" : qUnion([Q0]), "operationType" : NewBodyOperationType.ADD, "depth" : 7 * mm, "offsetDistance" : 25 * mm});
        }
        {
            var Q0;
            {var subQ0=sQuery(id+"F17.wireOp",EDGE,"E34");var subQ1=sQuery(id+"F0.wireOp",EDGE,"E0.right");var subQ2=makeQuery(id+"F1.opExtrude","SWEPT_EDGE",EDGE,{"disambiguationData":[OSD([sQuery(id+"F0.wireOp",EDGE,"E0.bottom"),subQ1])]});var subQ3=makeQuery(id+"F1.opExtrude","CAP_EDGE",EDGE,{"disambiguationData":[OSD([subQ1])],"isStart":false});var subQ5=makeQuery(id+"F13.imprint","IMPRINT",EDGE,{"disambiguationData":[TD([[makeQuery(id+"F13.imprint","INTERSECT",VERTEX,{"derivedFrom":[subQ3,subQ2]}),-1.0]])],"derivedFrom":subQ2});var subQ6=makeQuery(id+"F17.imprint","INTERSECT",VERTEX,{"derivedFrom":[subQ5,subQ0]});Q0=makeQuery(id+"F17.imprint","IMPRINT",FACE,{"disambiguationData":[TD([[makeQuery(id+"F17.imprint","IMPRINT",EDGE,{"disambiguationData":[TD([[subQ6,-1.0]])],"derivedFrom":subQ0}),1.0]])]});}
            extrude(context, id + "F29", {"entities" : qUnion([Q0]), "operationType" : NewBodyOperationType.ADD, "depth" : 7 * mm, "offsetDistance" : 25 * mm});
        }
        {
            var Q0;
            {var subQ1=sQuery(id+"F18.wireOp",EDGE,"E37");Q0=makeQuery(id+"F18.imprint","IMPRINT",FACE,{"disambiguationData":[TD([[makeQuery(id+"F18.imprint","IMPRINT",EDGE,{"derivedFrom":subQ1}),-1.0]])]});}
            extrude(context, id + "F30", {"entities" : qUnion([Q0]), "operationType" : NewBodyOperationType.ADD, "depth" : 7 * mm, "offsetDistance" : 25 * mm});
        }
        {
            var Q0;
            {var subQ0=sQuery(id+"F19.wireOp",EDGE,"E41");var subQ1=sQuery(id+"F0.wireOp",EDGE,"E0.left");var subQ2=makeQuery(id+"F1.opExtrude","SWEPT_EDGE",EDGE,{"disambiguationData":[OSD([sQuery(id+"F0.wireOp",EDGE,"E0.bottom"),subQ1])]});var subQ3=makeQuery(id+"F1.opExtrude","CAP_EDGE",EDGE,{"disambiguationData":[OSD([subQ1])],"isStart":false});var subQ5=makeQuery(id+"F11.imprint","IMPRINT",EDGE,{"disambiguationData":[TD([[makeQuery(id+"F11.imprint","INTERSECT",VERTEX,{"derivedFrom":[subQ3,subQ2]}),-1.0]])],"derivedFrom":subQ2});var subQ6=makeQuery(id+"F11.imprint","IMPRINT",EDGE,{"derivedFrom":subQ3});var subQ8=makeQuery(id+"F15.imprint","IMPRINT",EDGE,{"disambiguationData":[TD([[makeQuery(id+"F15.imprint","INTERSECT",VERTEX,{"derivedFrom":[subQ6,subQ5]}),-1.0]])],"derivedFrom":subQ5});var subQ9=makeQuery(id+"F19.imprint","INTERSECT",VERTEX,{"derivedFrom":[subQ8,subQ0]});Q0=makeQuery(id+"F19.imprint","IMPRINT",FACE,{"disambiguationData":[TD([[makeQuery(id+"F19.imprint","IMPRINT",EDGE,{"disambiguationData":[TD([[subQ9,1.0]])],"derivedFrom":subQ0}),1.0]])]});}
            extrude(context, id + "F31", {"entities" : qUnion([Q0]), "operationType" : NewBodyOperationType.ADD, "depth" : 7 * mm, "offsetDistance" : 25 * mm});
        }
        {
            var Q0;
            {var subQ0=sQuery(id+"F20.wireOp",EDGE,"E45");var subQ11=sQuery(id+"F20.wireOp",EDGE,"E43");var subQ12=makeQuery(id+"F20.imprint","INTERSECT",VERTEX,{"derivedFrom":[subQ11,subQ0]});Q0=makeQuery(id+"F20.imprint","IMPRINT",FACE,{"disambiguationData":[TD([[makeQuery(id+"F20.imprint","IMPRINT",EDGE,{"disambiguationData":[TD([[subQ12,-1.0]])],"derivedFrom":subQ11}),1.0]])]});}
            extrude(context, id + "F32", {"entities" : qUnion([Q0]), "operationType" : NewBodyOperationType.ADD, "depth" : 7 * mm, "offsetDistance" : 25 * mm});
        }
        {
            var Q0;
            {var subQ3=sQuery(id+"F0.wireOp",EDGE,"E0.right");var subQ5=makeQuery(id+"F1.opExtrude","CAP_EDGE",EDGE,{"disambiguationData":[OSD([subQ3])],"isStart":false});var subQ8=makeQuery(id+"F13.imprint","IMPRINT",EDGE,{"derivedFrom":subQ5});var subQ16=sQuery(id+"F21.wireOp",EDGE,"E46");var subQ18=makeQuery(id+"F17.imprint","IMPRINT",EDGE,{"derivedFrom":subQ8});var subQ20=makeQuery(id+"F21.imprint","INTERSECT",VERTEX,{"derivedFrom":[subQ18,subQ16]});Q0=makeQuery(id+"F21.imprint","IMPRINT",FACE,{"disambiguationData":[TD([[makeQuery(id+"F21.imprint","IMPRINT",EDGE,{"disambiguationData":[TD([[subQ20,1.0]])],"derivedFrom":subQ16}),1.0]])]});}
            extrude(context, id + "F33", {"entities" : qUnion([Q0]), "operationType" : NewBodyOperationType.ADD, "depth" : 7 * mm, "offsetDistance" : 25 * mm});
        }
        {
            var Q0;
            Q0=makeQuery(id+"F9.opExtrude","SWEPT_FACE",FACE,{"disambiguationData":[OSD([sQuery(id+"F2.wireOp",EDGE,"E1.bottom")])]});
            var sketch = newSketch(context, id + "F34", { "sketchPlane" : qUnion([Q0])});
            skCircle(sketch, "E51", {"center": v(0, 0) * mm, "radius": 20.4 * mm});
            skSolve(sketch);
        }
        {
            var Q0;
            {var subQ0=sQuery(id+"F34.wireOp",EDGE,"E51");var subQ1=makeQuery(id+"F9.opExtrude","CAP_EDGE",EDGE,{"disambiguationData":[OSD([sQuery(id+"F2.wireOp",EDGE,"E1.bottom")])],"isStart":true});var subQ2=makeQuery(id+"F34.imprint","INTERSECT",VERTEX,{"disambiguationData":[OD(0.0)],"derivedFrom":[subQ1,subQ0]});Q0=makeQuery(id+"F34.imprint","IMPRINT",FACE,{"disambiguationData":[TD([[makeQuery(id+"F34.imprint","IMPRINT",EDGE,{"disambiguationData":[TD([[subQ2,1.0]])],"derivedFrom":subQ0}),1.0]])]});}
            extrude(context, id + "F35", {"entities" : qUnion([Q0]), "operationType" : NewBodyOperationType.REMOVE, "oppositeDirection" : true, "depth" : 20 * mm, "offsetDistance" : 25 * mm});
        }
        {
            var Q0;
            Q0=makeQuery(id+"F9.opExtrude","SWEPT_FACE",FACE,{"disambiguationData":[OSD([sQuery(id+"F2.wireOp",EDGE,"E1.bottom")])]});
            var sketch = newSketch(context, id + "F36", { "sketchPlane" : qUnion([Q0])});
            skLineSegment(sketch, "E52", {"start": v(-91.64, 25.43) * mm, "end": v(91.64, 25.43) * mm});
            skLineSegment(sketch, "E53", {"start": v(91.64, 20.46) * mm, "end": v(-91.64, 20.36) * mm});
            skLineSegment(sketch, "E54", {"start": v(-91.64, 20.36) * mm, "end": v(-91.64, 15) * mm});
            skLineSegment(sketch, "E55", {"start": v(-91.64, 15) * mm, "end": v(-13.83, 15) * mm});
            skLineSegment(sketch, "E56", {"start": v(13.83, 15) * mm, "end": v(91.64, 15) * mm});
            skLineSegment(sketch, "E57", {"start": v(-91.64, 9.45) * mm, "end": v(-18.09, 9.45) * mm});
            skLineSegment(sketch, "E58", {"start": v(18.09, 9.45) * mm, "end": v(91.64, 9.45) * mm});
            skLineSegment(sketch, "E59", {"start": v(-91.64, 4.47) * mm, "end": v(-19.91, 4.47) * mm});
            skLineSegment(sketch, "E60", {"start": v(19.91, 4.47) * mm, "end": v(91.64, 4.47) * mm});
            skLineSegment(sketch, "E61", {"start": v(-78.25, 30) * mm, "end": v(-78.25, 25.43) * mm});
            skLineSegment(sketch, "E62", {"start": v(-84.54, 25.43) * mm, "end": v(-84.54, 20.36) * mm});
            skLineSegment(sketch, "E63", {"start": v(-52.3, 20.38) * mm, "end": v(-52.31, 25.43) * mm});
            skLineSegment(sketch, "E64", {"start": v(-62.8, 30) * mm, "end": v(-62.79, 25.43) * mm});
            skLineSegment(sketch, "E65", {"start": v(-75.37, 25.43) * mm, "end": v(-75.37, 20.36) * mm});
            skLineSegment(sketch, "E66", {"start": v(-70.65, 30) * mm, "end": v(-70.65, 25.43) * mm});
            skLineSegment(sketch, "E67", {"start": v(-39.47, 25.43) * mm, "end": v(-39.47, 30) * mm});
            skLineSegment(sketch, "E68", {"start": v(-66.2, 20.37) * mm, "end": v(-66.2, 15) * mm});
            skLineSegment(sketch, "E69", {"start": v(-78.25, 15) * mm, "end": v(-78.25, 9.45) * mm});
            skLineSegment(sketch, "E70", {"start": v(-84.54, 4.47) * mm, "end": v(-84.54, 0) * mm});
            skLineSegment(sketch, "E71", {"start": v(-82.18, 20.36) * mm, "end": v(-82.18, 15) * mm});
            skLineSegment(sketch, "E72", {"start": v(-58.34, 25.43) * mm, "end": v(-58.33, 20.36) * mm});
            skLineSegment(sketch, "E73", {"start": v(-71.18, 15) * mm, "end": v(-71.17, 9.45) * mm});
            skLineSegment(sketch, "E74", {"start": v(-82.18, 9.45) * mm, "end": v(-82.18, 4.47) * mm});
            skLineSegment(sketch, "E75", {"start": v(-46.02, 20.38) * mm, "end": v(-46.02, 15) * mm});
            skLineSegment(sketch, "E76", {"start": v(-52.3, 15) * mm, "end": v(-52.3, 9.45) * mm});
            skLineSegment(sketch, "E77", {"start": v(-66.2, 9.45) * mm, "end": v(-66.2, 4.47) * mm});
            skLineSegment(sketch, "E78", {"start": v(-75.37, 4.47) * mm, "end": v(-75.37, 0) * mm});
            skPoint(sketch, "E78.endSnap0", {"position": v(-56.02, 0) * mm});
            skLineSegment(sketch, "E79", {"start": v(-55.77, 4.47) * mm, "end": v(-56.02, 0) * mm});
            skLineSegment(sketch, "E80", {"start": v(-39.47, 20.38) * mm, "end": v(-39.47, 15) * mm});
            skLineSegment(sketch, "E81", {"start": v(-43.66, 9.45) * mm, "end": v(-43.66, 15) * mm});
            skLineSegment(sketch, "E82", {"start": v(-46.02, 9.45) * mm, "end": v(-46.01, 4.47) * mm});
            skLineSegment(sketch, "E83", {"start": v(-46.01, 4.47) * mm, "end": v(-47.85, 4.47) * mm});
            skLineSegment(sketch, "E84", {"start": v(-31.87, 0) * mm, "end": v(-31.87, 4.47) * mm});
            skLineSegment(sketch, "E85", {"start": v(-24.8, 30) * mm, "end": v(-24.8, 25.43) * mm});
            skLineSegment(sketch, "E86", {"start": v(-33.97, 25.43) * mm, "end": v(-33.96, 20.39) * mm});
            skLineSegment(sketch, "E87", {"start": v(-26.63, 15) * mm, "end": v(-26.63, 20.4) * mm});
            skLineSegment(sketch, "E88", {"start": v(-26.63, 20.4) * mm, "end": v(-27.68, 21.5) * mm});
            skLineSegment(sketch, "E89", {"start": v(-30.3, 15) * mm, "end": v(-30.3, 9.45) * mm});
            skLineSegment(sketch, "E90", {"start": v(-16.15, 30) * mm, "end": v(-16.14, 25.43) * mm});
            skLineSegment(sketch, "E91", {"start": v(-7.76, 25.43) * mm, "end": v(-7.76, 20.4) * mm});
            skLineSegment(sketch, "E92", {"start": v(-13.83, 15) * mm, "end": v(-13.84, 20.4) * mm});
            skLineSegment(sketch, "E93", {"start": v(6.65, 30) * mm, "end": v(6.65, 25.43) * mm});
            skLineSegment(sketch, "E94", {"start": v(0, 25.43) * mm, "end": v(0, 20.4) * mm});
            skLineSegment(sketch, "E95", {"start": v(0, 20.4) * mm, "end": v(1.15, 21.5) * mm});
            skLineSegment(sketch, "E96", {"start": v(14.25, 25.43) * mm, "end": v(14.25, 20.41) * mm});
            skLineSegment(sketch, "E97", {"start": v(14.25, 20.41) * mm, "end": v(12.42, 20.72) * mm});
            skLineSegment(sketch, "E98", {"start": v(13.83, 15) * mm, "end": v(14.25, 20.41) * mm});
            skLineSegment(sketch, "E99", {"start": v(11.37, 30) * mm, "end": v(11.37, 25.43) * mm});
            skLineSegment(sketch, "E100", {"start": v(27.1, 30) * mm, "end": v(27.1, 25.43) * mm});
            skLineSegment(sketch, "E101", {"start": v(27.1, 25.43) * mm, "end": v(20.4, 25.43) * mm});
            skLineSegment(sketch, "E102", {"start": v(20.4, 25.43) * mm, "end": v(20.4, 20.41) * mm});
            skLineSegment(sketch, "E103", {"start": v(25, 15) * mm, "end": v(25, 20.41) * mm});
            skLineSegment(sketch, "E104", {"start": v(27.1, 0) * mm, "end": v(27.1, 4.47) * mm});
            skLineSegment(sketch, "E105", {"start": v(34.95, 15) * mm, "end": v(34.96, 9.45) * mm});
            skLineSegment(sketch, "E106", {"start": v(31.55, 9.45) * mm, "end": v(31.55, 4.47) * mm});
            skLineSegment(sketch, "E107", {"start": v(40.46, 30) * mm, "end": v(40.46, 25.43) * mm});
            skLineSegment(sketch, "E108", {"start": v(35.48, 25.43) * mm, "end": v(35.48, 20.43) * mm});
            skLineSegment(sketch, "E109", {"start": v(44.91, 20.43) * mm, "end": v(44.91, 15) * mm});
            skLineSegment(sketch, "E110", {"start": v(52.77, 30) * mm, "end": v(52.78, 25.43) * mm});
            skLineSegment(sketch, "E111", {"start": v(57.75, 30) * mm, "end": v(57.75, 25.43) * mm});
            skLineSegment(sketch, "E112", {"start": v(48.06, 25.43) * mm, "end": v(48.06, 20.41) * mm});
            skLineSegment(sketch, "E113", {"start": v(41.77, 15) * mm, "end": v(41.77, 9.45) * mm});
            skLineSegment(sketch, "E114", {"start": v(38.62, 9.45) * mm, "end": v(38.62, 4.47) * mm});
            skLineSegment(sketch, "E115", {"start": v(61.94, 25.43) * mm, "end": v(61.95, 20.44) * mm});
            skLineSegment(sketch, "E116", {"start": v(55.4, 20.44) * mm, "end": v(55.4, 15) * mm});
            skLineSegment(sketch, "E117", {"start": v(55.4, 15) * mm, "end": v(54.08, 14.17) * mm});
            skLineSegment(sketch, "E118", {"start": v(52.78, 9.45) * mm, "end": v(52.77, 15) * mm});
            skLineSegment(sketch, "E119", {"start": v(52.77, 15) * mm, "end": v(54.08, 14.17) * mm});
            skLineSegment(sketch, "E120", {"start": v(35.74, 4.47) * mm, "end": v(35.74, 0) * mm});
            skLineSegment(sketch, "E121", {"start": v(47.8, 4.47) * mm, "end": v(47.8, 0) * mm});
            skLineSegment(sketch, "E122", {"start": v(62.73, 4.47) * mm, "end": v(62.73, 9.45) * mm});
            skLineSegment(sketch, "E123", {"start": v(62.73, 9.45) * mm, "end": v(64.04, 8.93) * mm});
            skLineSegment(sketch, "E124", {"start": v(55.77, 4.47) * mm, "end": v(55.78, 0) * mm});
            skLineSegment(sketch, "E125", {"start": v(70.07, 20.44) * mm, "end": v(70.07, 15) * mm});
            skLineSegment(sketch, "E126", {"start": v(74.78, 30) * mm, "end": v(74.79, 25.43) * mm});
            skLineSegment(sketch, "E127", {"start": v(73.47, 4.47) * mm, "end": v(73.47, 9.45) * mm});
            skLineSegment(sketch, "E128", {"start": v(70.07, 4.47) * mm, "end": v(70.07, 0) * mm});
            skLineSegment(sketch, "E129", {"start": v(65.35, 15) * mm, "end": v(65.35, 9.45) * mm});
            skLineSegment(sketch, "E130", {"start": v(65.35, 9.45) * mm, "end": v(66.92, 9.71) * mm});
            skLineSegment(sketch, "E131", {"start": v(83.96, 25.43) * mm, "end": v(83.96, 20.44) * mm});
            skLineSegment(sketch, "E132", {"start": v(67.97, 25.43) * mm, "end": v(67.97, 20.44) * mm});
            skLineSegment(sketch, "E133", {"start": v(78.72, 9.45) * mm, "end": v(78.71, 15) * mm});
            skLineSegment(sketch, "E134", {"start": v(88.94, 20.45) * mm, "end": v(88.94, 15) * mm});
            skLineSegment(sketch, "E135", {"start": v(88.94, 15) * mm, "end": v(87.1, 14.95) * mm});
            skLineSegment(sketch, "E136", {"start": v(83.96, 30) * mm, "end": v(83.96, 25.43) * mm});
            skLineSegment(sketch, "E137", {"start": v(80.03, 4.47) * mm, "end": v(80.03, 0) * mm});
            skLineSegment(sketch, "E138", {"start": v(86.31, 9.45) * mm, "end": v(86.32, 4.47) * mm});
            skLineSegment(sketch, "E139", {"start": v(22.82, 20.42) * mm, "end": v(22.82, 15) * mm});
            skSolve(sketch);
        }
        {
            var Q0;
            {var subQ5=sQuery(id+"F36.wireOp",EDGE,"E73");Q0=makeQuery(id+"F36.imprint","IMPRINT",FACE,{"disambiguationData":[TD([[makeQuery(id+"F36.imprint","IMPRINT",EDGE,{"derivedFrom":subQ5}),1.0]])]});}
            var Q1;
            {var subQ3=sQuery(id+"F36.wireOp",EDGE,"E89");Q1=makeQuery(id+"F36.imprint","IMPRINT",FACE,{"disambiguationData":[TD([[makeQuery(id+"F36.imprint","IMPRINT",EDGE,{"derivedFrom":subQ3}),1.0]])]});}
            var Q2;
            {var subQ6=sQuery(id+"F36.wireOp",EDGE,"E61");Q2=makeQuery(id+"F36.imprint","IMPRINT",FACE,{"disambiguationData":[TD([[makeQuery(id+"F36.imprint","IMPRINT",EDGE,{"derivedFrom":subQ6}),-1.0]])]});}
            var Q3;
            {var subQ4=sQuery(id+"F36.wireOp",EDGE,"E104");Q3=makeQuery(id+"F36.imprint","IMPRINT",FACE,{"disambiguationData":[TD([[makeQuery(id+"F36.imprint","IMPRINT",EDGE,{"derivedFrom":subQ4}),1.0]])]});}
            var Q4;
            {var subQ0=sQuery(id+"F36.wireOp",EDGE,"E120");Q4=makeQuery(id+"F36.imprint","IMPRINT",FACE,{"disambiguationData":[TD([[makeQuery(id+"F36.imprint","IMPRINT",EDGE,{"derivedFrom":subQ0}),1.0]])]});}
            var Q5;
            {var subQ0=sQuery(id+"F36.wireOp",EDGE,"E126");Q5=makeQuery(id+"F36.imprint","IMPRINT",FACE,{"disambiguationData":[TD([[makeQuery(id+"F36.imprint","IMPRINT",EDGE,{"derivedFrom":subQ0}),1.0]])]});}
            var Q6;
            {var subQ0=sQuery(id+"F36.wireOp",EDGE,"E110");Q6=makeQuery(id+"F36.imprint","IMPRINT",FACE,{"disambiguationData":[TD([[makeQuery(id+"F36.imprint","IMPRINT",EDGE,{"derivedFrom":subQ0}),1.0]])]});}
            var Q7;
            {var subQ0=sQuery(id+"F36.wireOp",EDGE,"E90");Q7=makeQuery(id+"F36.imprint","IMPRINT",FACE,{"disambiguationData":[TD([[makeQuery(id+"F36.imprint","IMPRINT",EDGE,{"derivedFrom":subQ0}),1.0]])]});}
            var Q8;
            {var subQ5=sQuery(id+"F36.wireOp",EDGE,"E127");Q8=makeQuery(id+"F36.imprint","IMPRINT",FACE,{"disambiguationData":[TD([[makeQuery(id+"F36.imprint","IMPRINT",EDGE,{"derivedFrom":subQ5}),-1.0]])]});}
            var Q9;
            {var subQ3=sQuery(id+"F36.wireOp",EDGE,"E109");Q9=makeQuery(id+"F36.imprint","IMPRINT",FACE,{"disambiguationData":[TD([[makeQuery(id+"F36.imprint","IMPRINT",EDGE,{"derivedFrom":subQ3}),1.0]])]});}
            var Q10;
            {var subQ3=sQuery(id+"F36.wireOp",EDGE,"E75");Q10=makeQuery(id+"F36.imprint","IMPRINT",FACE,{"disambiguationData":[TD([[makeQuery(id+"F36.imprint","IMPRINT",EDGE,{"derivedFrom":subQ3}),1.0]])]});}
            var Q11;
            {var subQ0=sQuery(id+"F36.wireOp",EDGE,"E70");Q11=makeQuery(id+"F36.imprint","IMPRINT",FACE,{"disambiguationData":[TD([[makeQuery(id+"F36.imprint","IMPRINT",EDGE,{"derivedFrom":subQ0}),1.0]])]});}
            var Q12;
            {var subQ0=sQuery(id+"F36.wireOp",EDGE,"E96");Q12=makeQuery(id+"F36.imprint","IMPRINT",FACE,{"disambiguationData":[TD([[makeQuery(id+"F36.imprint","IMPRINT",EDGE,{"derivedFrom":subQ0}),1.0]])]});}
            extrude(context, id + "F37", {"entities" : qUnion([Q0, Q1, Q2, Q3, Q4, Q5, Q6, Q7, Q8, Q9, Q10, Q11, Q12]), "operationType" : NewBodyOperationType.ADD, "depth" : 4 * mm, "offsetDistance" : 25 * mm});
        }
        {
            var Q0;
            {var subQ1=sQuery(id+"F36.wireOp",EDGE,"E54");Q0=makeQuery(id+"F36.imprint","IMPRINT",FACE,{"disambiguationData":[TD([[makeQuery(id+"F36.imprint","IMPRINT",EDGE,{"derivedFrom":subQ1}),1.0]])]});}
            var Q1;
            {var subQ0=sQuery(id+"F36.wireOp",EDGE,"E90");Q1=makeQuery(id+"F36.imprint","IMPRINT",FACE,{"disambiguationData":[TD([[makeQuery(id+"F36.imprint","IMPRINT",EDGE,{"derivedFrom":subQ0}),1.0]])]});}
            var Q2;
            {var subQ11=sQuery(id+"F36.wireOp",EDGE,"E137");Q2=makeQuery(id+"F36.imprint","IMPRINT",FACE,{"disambiguationData":[TD([[makeQuery(id+"F36.imprint","IMPRINT",EDGE,{"derivedFrom":subQ11}),1.0]])]});}
            var Q3;
            {var subQ5=sQuery(id+"F36.wireOp",EDGE,"E70");Q3=makeQuery(id+"F36.imprint","IMPRINT",FACE,{"disambiguationData":[TD([[makeQuery(id+"F36.imprint","IMPRINT",EDGE,{"derivedFrom":subQ5}),-1.0]])]});}
            var Q4;
            {var subQ0=sQuery(id+"F36.wireOp",EDGE,"E81");Q4=makeQuery(id+"F36.imprint","IMPRINT",FACE,{"disambiguationData":[TD([[makeQuery(id+"F36.imprint","IMPRINT",EDGE,{"derivedFrom":subQ0}),-1.0]])]});}
            var Q5;
            {var subQ0=sQuery(id+"F36.wireOp",EDGE,"E64");Q5=makeQuery(id+"F36.imprint","IMPRINT",FACE,{"disambiguationData":[TD([[makeQuery(id+"F36.imprint","IMPRINT",EDGE,{"derivedFrom":subQ0}),1.0]])]});}
            var Q6;
            {var subQ0=sQuery(id+"F36.wireOp",EDGE,"E120");Q6=makeQuery(id+"F36.imprint","IMPRINT",FACE,{"disambiguationData":[TD([[makeQuery(id+"F36.imprint","IMPRINT",EDGE,{"derivedFrom":subQ0}),1.0]])]});}
            var Q7;
            {var subQ0=sQuery(id+"F36.wireOp",EDGE,"E100");Q7=makeQuery(id+"F36.imprint","IMPRINT",FACE,{"disambiguationData":[TD([[makeQuery(id+"F36.imprint","IMPRINT",EDGE,{"derivedFrom":subQ0}),1.0]])]});}
            var Q8;
            {var subQ4=sQuery(id+"F36.wireOp",EDGE,"E84");Q8=makeQuery(id+"F36.imprint","IMPRINT",FACE,{"disambiguationData":[TD([[makeQuery(id+"F36.imprint","IMPRINT",EDGE,{"derivedFrom":subQ4}),-1.0]])]});}
            var Q9;
            {var subQ4=sQuery(id+"F36.wireOp",EDGE,"E104");Q9=makeQuery(id+"F36.imprint","IMPRINT",FACE,{"disambiguationData":[TD([[makeQuery(id+"F36.imprint","IMPRINT",EDGE,{"derivedFrom":subQ4}),1.0]])]});}
            var Q10;
            Q10=makeQuery(id+"F37.opExtrude","CAP_FACE",FACE,{"disambiguationData":[OSD([sQuery(id+"F2.wireOp",EDGE,"E1.bottom"),sQuery(id+"F36.wireOp",EDGE,"E52"),sQuery(id+"F36.wireOp",EDGE,"E90"),sQuery(id+"F36.wireOp",EDGE,"E93")])],"isStart":false});
            extrude(context, id + "F38", {"entities" : qUnion([Q0, Q1, Q2, Q3, Q4, Q5, Q6, Q7, Q8, Q9, Q10]), "operationType" : NewBodyOperationType.ADD, "depth" : 5 * mm, "offsetDistance" : 25 * mm});
        }
        {
            var Q0;
            {var subQ0=sQuery(id+"F36.wireOp",EDGE,"E68");Q0=makeQuery(id+"F36.imprint","IMPRINT",FACE,{"disambiguationData":[TD([[makeQuery(id+"F36.imprint","IMPRINT",EDGE,{"derivedFrom":subQ0}),1.0]])]});}
            var Q1;
            {var subQ3=sQuery(id+"F36.wireOp",EDGE,"E74");Q1=makeQuery(id+"F36.imprint","IMPRINT",FACE,{"disambiguationData":[TD([[makeQuery(id+"F36.imprint","IMPRINT",EDGE,{"derivedFrom":subQ3}),1.0]])]});}
            var Q2;
            {var subQ1=sQuery(id+"F36.wireOp",EDGE,"E79");Q2=makeQuery(id+"F36.imprint","IMPRINT",FACE,{"disambiguationData":[TD([[makeQuery(id+"F36.imprint","IMPRINT",EDGE,{"derivedFrom":subQ1}),1.0]])]});}
            var Q3;
            {var subQ6=sQuery(id+"F36.wireOp",EDGE,"E86");Q3=makeQuery(id+"F36.imprint","IMPRINT",FACE,{"disambiguationData":[TD([[makeQuery(id+"F36.imprint","IMPRINT",EDGE,{"derivedFrom":subQ6}),1.0]])]});}
            var Q4;
            {var subQ5=sQuery(id+"F36.wireOp",EDGE,"E106");Q4=makeQuery(id+"F36.imprint","IMPRINT",FACE,{"disambiguationData":[TD([[makeQuery(id+"F36.imprint","IMPRINT",EDGE,{"derivedFrom":subQ5}),1.0]])]});}
            var Q5;
            {var subQ5=sQuery(id+"F36.wireOp",EDGE,"E122");Q5=makeQuery(id+"F36.imprint","IMPRINT",FACE,{"disambiguationData":[TD([[makeQuery(id+"F36.imprint","IMPRINT",EDGE,{"derivedFrom":subQ5}),-1.0]])]});}
            var Q6;
            {var subQ8=sQuery(id+"F36.wireOp",EDGE,"E115");Q6=makeQuery(id+"F36.imprint","IMPRINT",FACE,{"disambiguationData":[TD([[makeQuery(id+"F36.imprint","IMPRINT",EDGE,{"derivedFrom":subQ8}),1.0]])]});}
            var Q7;
            {var subQ3=sQuery(id+"F36.wireOp",EDGE,"E134");Q7=makeQuery(id+"F36.imprint","IMPRINT",FACE,{"disambiguationData":[TD([[makeQuery(id+"F36.imprint","IMPRINT",EDGE,{"derivedFrom":subQ3}),1.0]])]});}
            var Q8;
            {var subQ1=sQuery(id+"F36.wireOp",EDGE,"E61");Q8=makeQuery(id+"F36.imprint","IMPRINT",FACE,{"disambiguationData":[TD([[makeQuery(id+"F36.imprint","IMPRINT",EDGE,{"derivedFrom":subQ1}),1.0]])]});}
            var Q9;
            {var subQ1=sQuery(id+"F36.wireOp",EDGE,"E101");Q9=makeQuery(id+"F36.imprint","IMPRINT",FACE,{"disambiguationData":[TD([[makeQuery(id+"F36.imprint","IMPRINT",EDGE,{"derivedFrom":subQ1}),1.0]])]});}
            var Q10;
            {var subQ0=sQuery(id+"F36.wireOp",EDGE,"E107");Q10=makeQuery(id+"F36.imprint","IMPRINT",FACE,{"disambiguationData":[TD([[makeQuery(id+"F36.imprint","IMPRINT",EDGE,{"derivedFrom":subQ0}),1.0]])]});}
            extrude(context, id + "F39", {"entities" : qUnion([Q0, Q1, Q2, Q3, Q4, Q5, Q6, Q7, Q8, Q9, Q10]), "operationType" : NewBodyOperationType.ADD, "depth" : 7 * mm, "offsetDistance" : 25 * mm});
        }
        {
            var Q0;
            {var subQ6=sQuery(id+"F36.wireOp",EDGE,"E63");Q0=makeQuery(id+"F36.imprint","IMPRINT",FACE,{"disambiguationData":[TD([[makeQuery(id+"F36.imprint","IMPRINT",EDGE,{"derivedFrom":subQ6}),-1.0]])]});}
            var Q1;
            {var subQ0=sQuery(id+"F36.wireOp",EDGE,"E69");Q1=makeQuery(id+"F36.imprint","IMPRINT",FACE,{"disambiguationData":[TD([[makeQuery(id+"F36.imprint","IMPRINT",EDGE,{"derivedFrom":subQ0}),1.0]])]});}
            var Q2;
            {var subQ6=sQuery(id+"F36.wireOp",EDGE,"E77");Q2=makeQuery(id+"F36.imprint","IMPRINT",FACE,{"disambiguationData":[TD([[makeQuery(id+"F36.imprint","IMPRINT",EDGE,{"derivedFrom":subQ6}),1.0]])]});}
            var Q3;
            {var subQ0=sQuery(id+"F36.wireOp",EDGE,"E105");Q3=makeQuery(id+"F36.imprint","IMPRINT",FACE,{"disambiguationData":[TD([[makeQuery(id+"F36.imprint","IMPRINT",EDGE,{"derivedFrom":subQ0}),-1.0]])]});}
            var Q4;
            {var subQ0=sQuery(id+"F36.wireOp",EDGE,"E121");Q4=makeQuery(id+"F36.imprint","IMPRINT",FACE,{"disambiguationData":[TD([[makeQuery(id+"F36.imprint","IMPRINT",EDGE,{"derivedFrom":subQ0}),1.0]])]});}
            var Q5;
            {var subQ7=sQuery(id+"F36.wireOp",EDGE,"E133");Q5=makeQuery(id+"F36.imprint","IMPRINT",FACE,{"disambiguationData":[TD([[makeQuery(id+"F36.imprint","IMPRINT",EDGE,{"derivedFrom":subQ7}),-1.0]])]});}
            var Q6;
            {var subQ4=sQuery(id+"F36.wireOp",EDGE,"E136");Q6=makeQuery(id+"F36.imprint","IMPRINT",FACE,{"disambiguationData":[TD([[makeQuery(id+"F36.imprint","IMPRINT",EDGE,{"derivedFrom":subQ4}),1.0]])]});}
            var Q7;
            {var subQ3=sQuery(id+"F36.wireOp",EDGE,"E53");var subQ5=makeQuery(id+"F36.imprint","INTERSECT",VERTEX,{"derivedFrom":[subQ3,sQuery(id+"F36.wireOp",EDGE,"E134")]});Q7=makeQuery(id+"F36.imprint","IMPRINT",FACE,{"disambiguationData":[TD([[makeQuery(id+"F36.imprint","IMPRINT",EDGE,{"disambiguationData":[TD([[subQ5,-1.0]])],"derivedFrom":subQ3}),-1.0]])]});}
            var Q8;
            {var subQ0=sQuery(id+"F36.wireOp",EDGE,"E94");Q8=makeQuery(id+"F36.imprint","IMPRINT",FACE,{"disambiguationData":[TD([[makeQuery(id+"F36.imprint","IMPRINT",EDGE,{"derivedFrom":subQ0}),1.0]])]});}
            var Q9;
            {var subQ0=sQuery(id+"F36.wireOp",EDGE,"E64");Q9=makeQuery(id+"F36.imprint","IMPRINT",FACE,{"disambiguationData":[TD([[makeQuery(id+"F36.imprint","IMPRINT",EDGE,{"derivedFrom":subQ0}),-1.0]])]});}
            var Q10;
            {var subQ0=sQuery(id+"F36.wireOp",EDGE,"E87");Q10=makeQuery(id+"F36.imprint","IMPRINT",FACE,{"disambiguationData":[TD([[makeQuery(id+"F36.imprint","IMPRINT",EDGE,{"derivedFrom":subQ0}),-1.0]])]});}
            var Q11;
            {var subQ0=sQuery(id+"F36.wireOp",EDGE,"E108");Q11=makeQuery(id+"F36.imprint","IMPRINT",FACE,{"disambiguationData":[TD([[makeQuery(id+"F36.imprint","IMPRINT",EDGE,{"derivedFrom":subQ0}),1.0]])]});}
            extrude(context, id + "F40", {"entities" : qUnion([Q0, Q1, Q2, Q3, Q4, Q5, Q6, Q7, Q8, Q9, Q10, Q11]), "operationType" : NewBodyOperationType.ADD, "depth" : 3 * mm, "offsetDistance" : 25 * mm});
        }
        {
            var Q0;
            {var subQ3=sQuery(id+"F36.wireOp",EDGE,"E80");Q0=makeQuery(id+"F36.imprint","IMPRINT",FACE,{"disambiguationData":[TD([[makeQuery(id+"F36.imprint","IMPRINT",EDGE,{"derivedFrom":subQ3}),1.0]])]});}
            var Q1;
            {var subQ0=sQuery(id+"F36.wireOp",EDGE,"E74");Q1=makeQuery(id+"F36.imprint","IMPRINT",FACE,{"disambiguationData":[TD([[makeQuery(id+"F36.imprint","IMPRINT",EDGE,{"derivedFrom":subQ0}),-1.0]])]});}
            var Q2;
            {var subQ0=sQuery(id+"F36.wireOp",EDGE,"E62");Q2=makeQuery(id+"F36.imprint","IMPRINT",FACE,{"disambiguationData":[TD([[makeQuery(id+"F36.imprint","IMPRINT",EDGE,{"derivedFrom":subQ0}),1.0]])]});}
            var Q3;
            {var subQ0=sQuery(id+"F36.wireOp",EDGE,"E63");Q3=makeQuery(id+"F36.imprint","IMPRINT",FACE,{"disambiguationData":[TD([[makeQuery(id+"F36.imprint","IMPRINT",EDGE,{"derivedFrom":subQ0}),1.0]])]});}
            var Q4;
            {var subQ5=sQuery(id+"F36.wireOp",EDGE,"E82");Q4=makeQuery(id+"F36.imprint","IMPRINT",FACE,{"disambiguationData":[TD([[makeQuery(id+"F36.imprint","IMPRINT",EDGE,{"derivedFrom":subQ5}),1.0]])]});}
            var Q5;
            {var subQ0=sQuery(id+"F36.wireOp",EDGE,"E106");Q5=makeQuery(id+"F36.imprint","IMPRINT",FACE,{"disambiguationData":[TD([[makeQuery(id+"F36.imprint","IMPRINT",EDGE,{"derivedFrom":subQ0}),-1.0]])]});}
            var Q6;
            {var subQ2=sQuery(id+"F36.wireOp",EDGE,"E115");Q6=makeQuery(id+"F36.imprint","IMPRINT",FACE,{"disambiguationData":[TD([[makeQuery(id+"F36.imprint","IMPRINT",EDGE,{"derivedFrom":subQ2}),-1.0]])]});}
            var Q7;
            {var subQ1=sQuery(id+"F36.wireOp",EDGE,"E128");Q7=makeQuery(id+"F36.imprint","IMPRINT",FACE,{"disambiguationData":[TD([[makeQuery(id+"F36.imprint","IMPRINT",EDGE,{"derivedFrom":subQ1}),1.0]])]});}
            var Q8;
            {var subQ0=sQuery(id+"F36.wireOp",EDGE,"E113");Q8=makeQuery(id+"F36.imprint","IMPRINT",FACE,{"disambiguationData":[TD([[makeQuery(id+"F36.imprint","IMPRINT",EDGE,{"derivedFrom":subQ0}),1.0]])]});}
            var Q9;
            {var subQ0=sQuery(id+"F36.wireOp",EDGE,"E93");Q9=makeQuery(id+"F36.imprint","IMPRINT",FACE,{"disambiguationData":[TD([[makeQuery(id+"F36.imprint","IMPRINT",EDGE,{"derivedFrom":subQ0}),1.0]])]});}
            var Q10;
            {var subQ0=sQuery(id+"F36.wireOp",EDGE,"E85");Q10=makeQuery(id+"F36.imprint","IMPRINT",FACE,{"disambiguationData":[TD([[makeQuery(id+"F36.imprint","IMPRINT",EDGE,{"derivedFrom":subQ0}),1.0]])]});}
            var Q11;
            Q11=makeQuery(id+"F40.opExtrude","CAP_FACE",FACE,{"disambiguationData":[OSD([sQuery(id+"F2.wireOp",EDGE,"E1.bottom"),sQuery(id+"F2.wireOp",EDGE,"E1.right"),sQuery(id+"F36.wireOp",EDGE,"E53"),sQuery(id+"F36.wireOp",EDGE,"E131"),sQuery(id+"F36.wireOp",EDGE,"E136")])],"isStart":false});
            var Q12;
            {var subQ0=sQuery(id+"F36.wireOp",EDGE,"E125");Q12=makeQuery(id+"F36.imprint","IMPRINT",FACE,{"disambiguationData":[TD([[makeQuery(id+"F36.imprint","IMPRINT",EDGE,{"derivedFrom":subQ0}),1.0]])]});}
            extrude(context, id + "F41", {"entities" : qUnion([Q0, Q1, Q2, Q3, Q4, Q5, Q6, Q7, Q8, Q9, Q10, Q11, Q12]), "operationType" : NewBodyOperationType.ADD, "depth" : 5.8 * mm, "offsetDistance" : 25 * mm});
        }
        {
            var Q0;
            {var subQ0=sQuery(id+"F36.wireOp",EDGE,"E98");Q0=makeQuery(id+"F36.imprint","IMPRINT",FACE,{"disambiguationData":[TD([[makeQuery(id+"F36.imprint","IMPRINT",EDGE,{"derivedFrom":subQ0}),-1.0]])]});}
            var Q1;
            {var subQ1=sQuery(id+"F36.wireOp",EDGE,"E124");Q1=makeQuery(id+"F36.imprint","IMPRINT",FACE,{"disambiguationData":[TD([[makeQuery(id+"F36.imprint","IMPRINT",EDGE,{"derivedFrom":subQ1}),1.0]])]});}
            var Q2;
            {var subQ3=sQuery(id+"F36.wireOp",EDGE,"E116");Q2=makeQuery(id+"F36.imprint","IMPRINT",FACE,{"disambiguationData":[TD([[makeQuery(id+"F36.imprint","IMPRINT",EDGE,{"derivedFrom":subQ3}),1.0]])]});}
            var Q3;
            {var subQ0=sQuery(id+"F36.wireOp",EDGE,"E105");Q3=makeQuery(id+"F36.imprint","IMPRINT",FACE,{"disambiguationData":[TD([[makeQuery(id+"F36.imprint","IMPRINT",EDGE,{"derivedFrom":subQ0}),1.0]])]});}
            var Q4;
            {var subQ6=sQuery(id+"F36.wireOp",EDGE,"E68");Q4=makeQuery(id+"F36.imprint","IMPRINT",FACE,{"disambiguationData":[TD([[makeQuery(id+"F36.imprint","IMPRINT",EDGE,{"derivedFrom":subQ6}),-1.0]])]});}
            var Q5;
            {var subQ0=sQuery(id+"F36.wireOp",EDGE,"E78");Q5=makeQuery(id+"F36.imprint","IMPRINT",FACE,{"disambiguationData":[TD([[makeQuery(id+"F36.imprint","IMPRINT",EDGE,{"derivedFrom":subQ0}),1.0]])]});}
            var Q6;
            {var subQ0=sQuery(id+"F36.wireOp",EDGE,"E69");Q6=makeQuery(id+"F36.imprint","IMPRINT",FACE,{"disambiguationData":[TD([[makeQuery(id+"F36.imprint","IMPRINT",EDGE,{"derivedFrom":subQ0}),-1.0]])]});}
            var Q7;
            {var subQ3=sQuery(id+"F36.wireOp",EDGE,"E67");Q7=makeQuery(id+"F36.imprint","IMPRINT",FACE,{"disambiguationData":[TD([[makeQuery(id+"F36.imprint","IMPRINT",EDGE,{"derivedFrom":subQ3}),-1.0]])]});}
            var Q8;
            {var subQ1=sQuery(id+"F36.wireOp",EDGE,"E99");Q8=makeQuery(id+"F36.imprint","IMPRINT",FACE,{"disambiguationData":[TD([[makeQuery(id+"F36.imprint","IMPRINT",EDGE,{"derivedFrom":subQ1}),1.0]])]});}
            var Q9;
            {var subQ3=sQuery(id+"F36.wireOp",EDGE,"E111");Q9=makeQuery(id+"F36.imprint","IMPRINT",FACE,{"disambiguationData":[TD([[makeQuery(id+"F36.imprint","IMPRINT",EDGE,{"derivedFrom":subQ3}),1.0]])]});}
            extrude(context, id + "F42", {"entities" : qUnion([Q0, Q1, Q2, Q3, Q4, Q5, Q6, Q7, Q8, Q9]), "operationType" : NewBodyOperationType.ADD, "depth" : 4.5 * mm, "offsetDistance" : 25 * mm});
        }
        {
            var Q0;
            {var subQ0=sQuery(id+"F36.wireOp",EDGE,"E117");Q0=makeQuery(id+"F36.imprint","IMPRINT",FACE,{"disambiguationData":[TD([[makeQuery(id+"F36.imprint","IMPRINT",EDGE,{"derivedFrom":subQ0}),1.0]])]});}
            extrude(context, id + "F43", {"entities" : qUnion([Q0]), "operationType" : NewBodyOperationType.ADD, "depth" : 3.5 * mm, "offsetDistance" : 25 * mm});
        }
        {
            var Q0;
            {var subQ0=sQuery(id+"F36.wireOp",EDGE,"E69");Q0=makeQuery(id+"F36.imprint","IMPRINT",FACE,{"disambiguationData":[TD([[makeQuery(id+"F36.imprint","IMPRINT",EDGE,{"derivedFrom":subQ0}),-1.0]])]});}
            extrude(context, id + "F44", {"entities" : qUnion([Q0]), "operationType" : NewBodyOperationType.ADD, "depth" : 5.5 * mm, "offsetDistance" : 25 * mm});
        }
        {
            var Q0;
            {var subQ0=sQuery(id+"F0.wireOp",EDGE,"E0.left");var subQ1=sQuery(id+"F0.wireOp",EDGE,"E0.top");var subQ2=sQuery(id+"F0.wireOp",EDGE,"E0.right");var subQ4=sQuery(id+"F21.wireOp",EDGE,"E47");Q0=makeQuery(id+"F31.boolean.opBoolean","MERGE",FACE,{"derivedFrom":[makeQuery(id+"F29.boolean.opBoolean","MERGE",FACE,{"derivedFrom":[makeQuery(id+"F27.boolean.opBoolean","MERGE",FACE,{"derivedFrom":[makeQuery(id+"F26.boolean.opBoolean","SPLIT",FACE,{"disambiguationData":[TD([makeQuery(id+"F22.opExtrude","SWEPT_FACE",FACE,{"disambiguationData":[OSD([subQ4])]})])],"derivedFrom":makeQuery(id+"F25.boolean.opBoolean","MERGE",FACE,{"derivedFrom":[makeQuery(id+"F22.boolean.opBoolean","MERGE",FACE,{"derivedFrom":[makeQuery(id+"F1.opExtrude","SWEPT_FACE",FACE,{"disambiguationData":[OSD([subQ1])]}),makeQuery(id+"F22.opExtrude","SWEPT_FACE",FACE,{"disambiguationData":[OSD([subQ1,subQ0])]})]}),makeQuery(id+"F25.opExtrude","SWEPT_FACE",FACE,{"disambiguationData":[OSD([subQ1,subQ2])]})]})}),makeQuery(id+"F27.opExtrude","SWEPT_FACE",FACE,{"disambiguationData":[OSD([subQ1,subQ0])]})]}),makeQuery(id+"F29.opExtrude","SWEPT_FACE",FACE,{"disambiguationData":[OSD([subQ1,subQ2])]})]}),makeQuery(id+"F31.opExtrude","SWEPT_FACE",FACE,{"disambiguationData":[OSD([subQ1,subQ0])]})]});}
            var sketch = newSketch(context, id + "F45", { "sketchPlane" : qUnion([Q0])});
            skText(sketch, "E140", { "text": "SW", "fontName": "Tinos-Bold.ttf"});
            const initialGuessF45  = {"E140": [-0.04075, 0.5489, 1, 0, 0.03967]};
            skSetInitialGuess(sketch, initialGuessF45);
            skSolve(sketch);
        }
        {
            var Q0;
            Q0=makeQuery(id+"F45.imprint","IMPRINT",FACE,{"disambiguationData":[TD([[makeQuery(id+"F45.imprint","IMPRINT",EDGE,{"derivedFrom":sQuery(id+"F45.wireOp",EDGE,"E140.sketch_text.stroke-0")}),-1.0]])]});
            var Q1;
            Q1=makeQuery(id+"F45.imprint","IMPRINT",FACE,{"disambiguationData":[TD([[makeQuery(id+"F45.imprint","IMPRINT",EDGE,{"derivedFrom":sQuery(id+"F45.wireOp",EDGE,"E140.sketch_text.stroke-29")}),-1.0]])]});
            extrude(context, id + "F46", {"entities" : qUnion([Q0, Q1]), "operationType" : NewBodyOperationType.ADD, "depth" : 15 * mm, "offsetDistance" : 25 * mm});
        }
        {
            var Q0;
            {var subQ0=sQuery(id+"F3.wireOp",EDGE,"E2.left");var subQ1=sQuery(id+"F3.wireOp",EDGE,"E2.top");var subQ2=sQuery(id+"F3.wireOp",EDGE,"E2.right");var subQ3=sQuery(id+"F3.wireOp",EDGE,"E2.bottom");var subQ4=sQuery(id+"F5.wireOp",EDGE,"E4");Q0=makeQuery(id+"F6.boolean.opBoolean","SPLIT",FACE,{"disambiguationData":[TD([makeQuery(id+"F4.opExtrude","SWEPT_FACE",FACE,{"disambiguationData":[OSD([subQ3])]}),makeQuery(id+"F4.opExtrude","SWEPT_FACE",FACE,{"disambiguationData":[OSD([subQ1])]}),makeQuery(id+"F4.opExtrude","SWEPT_FACE",FACE,{"disambiguationData":[OSD([subQ0])]}),makeQuery(id+"F4.opExtrude","SWEPT_FACE",FACE,{"disambiguationData":[OSD([subQ2])]}),makeQuery(id+"F6.opExtrude","CAP_FACE",FACE,{"disambiguationData":[OSD([sQuery(id+"F5.wireOp",EDGE,"E3"),subQ4])],"isStart":true}),makeQuery(id+"F6.opExtrude","SWEPT_FACE",FACE,{"disambiguationData":[OSD([subQ4])]})])],"derivedFrom":makeQuery(id+"F4.opExtrude","CAP_FACE",FACE,{"disambiguationData":[OSD([subQ3,subQ1,subQ0,subQ2])],"isStart":false})});}
            var sketch = newSketch(context, id + "F47", { "sketchPlane" : qUnion([Q0])});
            skLineSegment(sketch, "E141.bottom", {"start": v(-28.38, 43.04) * mm, "end": v(26.93, 43.04) * mm});
            skLineSegment(sketch, "E141.top", {"start": v(-28.38, 23.52) * mm, "end": v(26.93, 23.52) * mm});
            skLineSegment(sketch, "E141.left", {"start": v(-28.38, 43.04) * mm, "end": v(-28.38, 23.52) * mm});
            skLineSegment(sketch, "E141.right", {"start": v(26.93, 43.04) * mm, "end": v(26.93, 23.52) * mm});
            skLineSegment(sketch, "E142.bottom", {"start": v(-31.4, 46.34) * mm, "end": v(29.95, 46.34) * mm});
            skLineSegment(sketch, "E142.top", {"start": v(-31.4, 21.29) * mm, "end": v(29.95, 21.29) * mm});
            skLineSegment(sketch, "E142.left", {"start": v(-31.4, 46.34) * mm, "end": v(-31.4, 21.29) * mm});
            skLineSegment(sketch, "E142.right", {"start": v(29.95, 46.34) * mm, "end": v(29.95, 21.29) * mm});
            skPoint(sketch, "E142.middle", {"position": v(-0.72, 33.81) * mm});
            skPoint(sketch, "E142.middle.positionSnap0", {"position": v(-0.72, 43.04) * mm});
            skPoint(sketch, "E142.centerSnap0", {"position": v(-0.72, 43.04) * mm});
            skLineSegment(sketch, "E143.bottom", {"start": v(-47.18, 13.4) * mm, "end": v(-29.46, 13.4) * mm});
            skLineSegment(sketch, "E143.top", {"start": v(-47.18, -33.24) * mm, "end": v(-29.46, -33.24) * mm});
            skLineSegment(sketch, "E143.left", {"start": v(-47.18, 13.4) * mm, "end": v(-47.18, -33.24) * mm});
            skLineSegment(sketch, "E143.right", {"start": v(-29.46, 13.4) * mm, "end": v(-29.46, -33.24) * mm});
            skLineSegment(sketch, "E144.bottom", {"start": v(-12.59, -8.5) * mm, "end": v(-23.2, -8.5) * mm});
            skLineSegment(sketch, "E144.top", {"start": v(-12.59, 8.5) * mm, "end": v(-23.2, 8.5) * mm});
            skLineSegment(sketch, "E144.left", {"start": v(-12.59, -8.5) * mm, "end": v(-12.59, 8.5) * mm});
            skLineSegment(sketch, "E144.right", {"start": v(-23.2, -8.5) * mm, "end": v(-23.2, 8.5) * mm});
            skPoint(sketch, "E144.middle", {"position": v(-17.9, 0) * mm});
            skLineSegment(sketch, "E145.bottom", {"start": v(-12.83, -11.91) * mm, "end": v(-23.32, -11.91) * mm});
            skLineSegment(sketch, "E145.top", {"start": v(-12.83, -29.63) * mm, "end": v(-23.32, -29.63) * mm});
            skLineSegment(sketch, "E145.left", {"start": v(-12.83, -11.91) * mm, "end": v(-12.83, -29.63) * mm});
            skLineSegment(sketch, "E145.right", {"start": v(-23.32, -11.91) * mm, "end": v(-23.32, -29.63) * mm});
            skPoint(sketch, "E145.middle", {"position": v(-18.08, -20.77) * mm});
            skSolve(sketch);
        }
        {
            var Q0;
            Q0=makeQuery(id+"F47.imprint","IMPRINT",FACE,{"disambiguationData":[TD([[makeQuery(id+"F47.imprint","IMPRINT",EDGE,{"derivedFrom":sQuery(id+"F47.wireOp",EDGE,"E141.bottom")}),-1.0]])]});
            extrude(context, id + "F48", {"entities" : qUnion([Q0]), "operationType" : NewBodyOperationType.REMOVE, "oppositeDirection" : true, "depth" : 25 * mm, "offsetDistance" : 25 * mm});
        }
        {
            var Q0;
            Q0=makeQuery(id+"F47.imprint","IMPRINT",FACE,{"disambiguationData":[TD([[makeQuery(id+"F47.imprint","IMPRINT",EDGE,{"derivedFrom":sQuery(id+"F47.wireOp",EDGE,"E141.bottom")}),1.0]])]});
            extrude(context, id + "F49", {"entities" : qUnion([Q0]), "operationType" : NewBodyOperationType.ADD, "depth" : 5 * mm, "offsetDistance" : 25 * mm});
        }
        {
            var Q0;
            Q0=makeQuery(id+"F47.imprint","IMPRINT",FACE,{"disambiguationData":[TD([[makeQuery(id+"F47.imprint","IMPRINT",EDGE,{"derivedFrom":sQuery(id+"F47.wireOp",EDGE,"E143.bottom")}),-1.0]])]});
            extrude(context, id + "F50", {"entities" : qUnion([Q0]), "operationType" : NewBodyOperationType.ADD, "depth" : 30 * mm, "offsetDistance" : 25 * mm});
        }
        {
            var Q0;
            Q0=makeQuery(id+"F50.opExtrude","SWEPT_FACE",FACE,{"disambiguationData":[OSD([sQuery(id+"F47.wireOp",EDGE,"E143.right")])]});
            var sketch = newSketch(context, id + "F51", { "sketchPlane" : qUnion([Q0])});
            skLineSegment(sketch, "E146.bottom", {"start": v(-33.24, 640) * mm, "end": v(13.4, 640) * mm});
            skLineSegment(sketch, "E146.top", {"start": v(-33.24, 650.62) * mm, "end": v(13.4, 650.62) * mm});
            skLineSegment(sketch, "E146.left", {"start": v(-33.24, 640) * mm, "end": v(-33.24, 650.62) * mm});
            skLineSegment(sketch, "E146.right", {"start": v(13.4, 640) * mm, "end": v(13.4, 650.62) * mm});
            skSolve(sketch);
        }
        {
            var Q0;
            Q0=makeQuery(id+"F51.imprint","IMPRINT",FACE,{"disambiguationData":[TD([[makeQuery(id+"F51.imprint","IMPRINT",EDGE,{"derivedFrom":sQuery(id+"F51.wireOp",EDGE,"E146.bottom")}),1.0]])]});
            extrude(context, id + "F52", {"entities" : qUnion([Q0]), "operationType" : NewBodyOperationType.REMOVE, "oppositeDirection" : true, "depth" : 9 * mm, "offsetDistance" : 25 * mm});
        }
        {
            var Q0;
            Q0=makeQuery(id+"F47.imprint","IMPRINT",FACE,{"disambiguationData":[TD([[makeQuery(id+"F47.imprint","IMPRINT",EDGE,{"derivedFrom":sQuery(id+"F47.wireOp",EDGE,"E144.bottom")}),-1.0]])]});
            var Q1;
            Q1=makeQuery(id+"F47.imprint","IMPRINT",FACE,{"disambiguationData":[TD([[makeQuery(id+"F47.imprint","IMPRINT",EDGE,{"derivedFrom":sQuery(id+"F47.wireOp",EDGE,"E145.bottom")}),1.0]])]});
            extrude(context, id + "F53", {"entities" : qUnion([Q0, Q1]), "operationType" : NewBodyOperationType.ADD, "depth" : 10 * mm, "offsetDistance" : 25 * mm});
        }
        {
            var Q0;
            {var subQ0=sQuery(id+"F2.wireOp",EDGE,"E1.left");Q0=makeQuery(id+"F37.boolean.opBoolean","MERGE",EDGE,{"derivedFrom":[makeQuery(id+"F9.opExtrude","CAP_EDGE",EDGE,{"disambiguationData":[OSD([subQ0])],"isStart":false}),makeQuery(id+"F37.opExtrude","SWEPT_EDGE",EDGE,{"disambiguationData":[OSD([sQuery(id+"F2.wireOp",EDGE,"E1.bottom"),subQ0])]})]});}
            var Q1;
            {var subQ0=sQuery(id+"F2.wireOp",EDGE,"E1.right");var subQ1=sQuery(id+"F2.wireOp",EDGE,"E1.bottom");Q1=makeQuery(id+"F41.boolean.opBoolean","MERGE",EDGE,{"derivedFrom":[makeQuery(id+"F40.boolean.opBoolean","MERGE",EDGE,{"derivedFrom":[makeQuery(id+"F9.opExtrude","CAP_EDGE",EDGE,{"disambiguationData":[OSD([subQ0])],"isStart":false}),makeQuery(id+"F40.opExtrude","SWEPT_EDGE",EDGE,{"disambiguationData":[OSD([subQ1,subQ0])]})]}),makeQuery(id+"F41.opExtrude","SWEPT_EDGE",EDGE,{"disambiguationData":[OSD([subQ1,subQ0])]})]});}
            var Q2;
            Q2=makeQuery(id+"F9.opExtrude","CAP_EDGE",EDGE,{"disambiguationData":[OSD([sQuery(id+"F2.wireOp",EDGE,"E1.top")])],"isStart":false});
            chamfer(context, id + "F54", {"entities" : qUnion([Q0, Q1, Q2]), "width" : 10 * mm, "tangentPropagation" : true});
        }
        {
            var Q0;
            Q0=makeQuery(id+"F4.opExtrude","SWEPT_FACE",FACE,{"disambiguationData":[OSD([sQuery(id+"F3.wireOp",EDGE,"E2.top")])]});
            var sketch = newSketch(context, id + "F55", { "sketchPlane" : qUnion([Q0])});
            skLineSegment(sketch, "E147", {"start": v(-34.4, 625) * mm, "end": v(-34.4, 600) * mm});
            skLineSegment(sketch, "E148", {"start": v(-15.45, 625) * mm, "end": v(-15.45, 600) * mm});
            skLineSegment(sketch, "E149", {"start": v(2.76, 625) * mm, "end": v(2.76, 600) * mm});
            skLineSegment(sketch, "E150", {"start": v(23.56, 625) * mm, "end": v(23.56, 600) * mm});
            skLineSegment(sketch, "E151", {"start": v(38.68, 625) * mm, "end": v(38.68, 600) * mm});
            skSolve(sketch);
        }
        {
            var Q0;
            {var subQ4=sQuery(id+"F55.wireOp",EDGE,"E147");Q0=makeQuery(id+"F55.imprint","IMPRINT",FACE,{"disambiguationData":[TD([[makeQuery(id+"F55.imprint","IMPRINT",EDGE,{"derivedFrom":subQ4}),-1.0]])]});}
            var Q1;
            {var subQ0=sQuery(id+"F55.wireOp",EDGE,"E148");Q1=makeQuery(id+"F55.imprint","IMPRINT",FACE,{"disambiguationData":[TD([[makeQuery(id+"F55.imprint","IMPRINT",EDGE,{"derivedFrom":subQ0}),1.0]])]});}
            var Q2;
            {var subQ0=sQuery(id+"F55.wireOp",EDGE,"E150");Q2=makeQuery(id+"F55.imprint","IMPRINT",FACE,{"disambiguationData":[TD([[makeQuery(id+"F55.imprint","IMPRINT",EDGE,{"derivedFrom":subQ0}),1.0]])]});}
            extrude(context, id + "F56", {"entities" : qUnion([Q0, Q1, Q2]), "operationType" : NewBodyOperationType.ADD, "depth" : 1 * mm, "offsetDistance" : 25 * mm});
        }
        {
            var Q0;
            {var subQ4=sQuery(id+"F3.wireOp",EDGE,"E2.top");var subQ6=makeQuery(id+"F4.opExtrude","SWEPT_FACE",FACE,{"disambiguationData":[OSD([subQ4])]});Q0=makeQuery(id+"F56.boolean.opBoolean","SPLIT",FACE,{"disambiguationData":[TD([makeQuery(id+"F56.opExtrude","SWEPT_FACE",FACE,{"disambiguationData":[OSD([sQuery(id+"F55.wireOp",EDGE,"E147")])]})])],"derivedFrom":subQ6});}
            var Q1;
            {var subQ3=sQuery(id+"F3.wireOp",EDGE,"E2.top");var subQ5=sQuery(id+"F55.wireOp",EDGE,"E149");var subQ6=makeQuery(id+"F4.opExtrude","SWEPT_FACE",FACE,{"disambiguationData":[OSD([subQ3])]});Q1=makeQuery(id+"F56.boolean.opBoolean","SPLIT",FACE,{"disambiguationData":[TD([makeQuery(id+"F56.opExtrude","SWEPT_FACE",FACE,{"disambiguationData":[OSD([subQ5])]})])],"derivedFrom":subQ6});}
            var Q2;
            {var subQ1=sQuery(id+"F3.wireOp",EDGE,"E2.right");var subQ2=sQuery(id+"F3.wireOp",EDGE,"E2.top");Q2=makeQuery(id+"F56.boolean.opBoolean","SPLIT",FACE,{"disambiguationData":[TD([makeQuery(id+"F4.opExtrude","SWEPT_FACE",FACE,{"disambiguationData":[OSD([subQ1])]})])],"derivedFrom":makeQuery(id+"F4.opExtrude","SWEPT_FACE",FACE,{"disambiguationData":[OSD([subQ2])]})});}
            extrude(context, id + "F57", {"entities" : qUnion([Q0, Q1, Q2]), "operationType" : NewBodyOperationType.ADD, "depth" : 2 * mm, "offsetDistance" : 25 * mm});
        }
        {
            var Q0;
            {var subQ0=sQuery(id+"F3.wireOp",EDGE,"E2.left");Q0=makeQuery(id+"F56.boolean.opBoolean","MERGE",FACE,{"derivedFrom":[makeQuery(id+"F4.opExtrude","SWEPT_FACE",FACE,{"disambiguationData":[OSD([subQ0])]}),makeQuery(id+"F56.opExtrude","SWEPT_FACE",FACE,{"disambiguationData":[OSD([sQuery(id+"F3.wireOp",EDGE,"E2.top"),subQ0])]})]});}
            var sketch = newSketch(context, id + "F58", { "sketchPlane" : qUnion([Q0])});
            skLineSegment(sketch, "E152", {"start": v(-33.8, 625) * mm, "end": v(-33.8, 600) * mm});
            skLineSegment(sketch, "E153", {"start": v(-12.91, 625) * mm, "end": v(-12.91, 600) * mm});
            skLineSegment(sketch, "E154", {"start": v(5.75, 625) * mm, "end": v(5.75, 600) * mm});
            skLineSegment(sketch, "E155", {"start": v(29.5, 625) * mm, "end": v(29.5, 600) * mm});
            skSolve(sketch);
        }
        {
            var Q0;
            {var subQ10=sQuery(id+"F58.wireOp",EDGE,"E152");Q0=makeQuery(id+"F58.imprint","IMPRINT",FACE,{"disambiguationData":[TD([[makeQuery(id+"F58.imprint","IMPRINT",EDGE,{"derivedFrom":subQ10}),-1.0]])]});}
            var Q1;
            {var subQ0=sQuery(id+"F58.wireOp",EDGE,"E153");Q1=makeQuery(id+"F58.imprint","IMPRINT",FACE,{"disambiguationData":[TD([[makeQuery(id+"F58.imprint","IMPRINT",EDGE,{"derivedFrom":subQ0}),1.0]])]});}
            var Q2;
            {var subQ13=sQuery(id+"F58.wireOp",EDGE,"E155");Q2=makeQuery(id+"F58.imprint","IMPRINT",FACE,{"disambiguationData":[TD([[makeQuery(id+"F58.imprint","IMPRINT",EDGE,{"derivedFrom":subQ13}),1.0]])]});}
            extrude(context, id + "F59", {"entities" : qUnion([Q0, Q1, Q2]), "operationType" : NewBodyOperationType.ADD, "depth" : 2 * mm, "offsetDistance" : 25 * mm});
        }
        {
            var Q0;
            {var subQ3=sQuery(id+"F3.wireOp",EDGE,"E2.left");var subQ4=sQuery(id+"F3.wireOp",EDGE,"E2.top");var subQ13=makeQuery(id+"F4.opExtrude","SWEPT_FACE",FACE,{"disambiguationData":[OSD([subQ3])]});Q0=makeQuery(id+"F59.boolean.opBoolean","SPLIT",FACE,{"disambiguationData":[TD([makeQuery(id+"F59.opExtrude","SWEPT_FACE",FACE,{"disambiguationData":[OSD([sQuery(id+"F58.wireOp",EDGE,"E152")])]})])],"derivedFrom":makeQuery(id+"F56.boolean.opBoolean","MERGE",FACE,{"derivedFrom":[subQ13,makeQuery(id+"F56.opExtrude","SWEPT_FACE",FACE,{"disambiguationData":[OSD([subQ4,subQ3])]})]})});}
            var Q1;
            {var subQ3=sQuery(id+"F3.wireOp",EDGE,"E2.left");var subQ4=sQuery(id+"F3.wireOp",EDGE,"E2.top");var subQ12=sQuery(id+"F58.wireOp",EDGE,"E154");var subQ13=makeQuery(id+"F4.opExtrude","SWEPT_FACE",FACE,{"disambiguationData":[OSD([subQ3])]});Q1=makeQuery(id+"F59.boolean.opBoolean","SPLIT",FACE,{"disambiguationData":[TD([makeQuery(id+"F59.opExtrude","SWEPT_FACE",FACE,{"disambiguationData":[OSD([subQ12])]})])],"derivedFrom":makeQuery(id+"F56.boolean.opBoolean","MERGE",FACE,{"derivedFrom":[subQ13,makeQuery(id+"F56.opExtrude","SWEPT_FACE",FACE,{"disambiguationData":[OSD([subQ4,subQ3])]})]})});}
            extrude(context, id + "F60", {"entities" : qUnion([Q0, Q1]), "operationType" : NewBodyOperationType.ADD, "depth" : 1 * mm, "offsetDistance" : 25 * mm});
        }
        {
            var Q0;
            {var subQ0=sQuery(id+"F3.wireOp",EDGE,"E2.right");Q0=makeQuery(id+"F57.boolean.opBoolean","MERGE",FACE,{"derivedFrom":[makeQuery(id+"F4.opExtrude","SWEPT_FACE",FACE,{"disambiguationData":[OSD([subQ0])]}),makeQuery(id+"F57.opExtrude","SWEPT_FACE",FACE,{"disambiguationData":[OSD([sQuery(id+"F3.wireOp",EDGE,"E2.top"),subQ0])]})]});}
            var sketch = newSketch(context, id + "F61", { "sketchPlane" : qUnion([Q0])});
            skLineSegment(sketch, "E156", {"start": v(-33.8, 625) * mm, "end": v(-33.8, 600) * mm});
            skLineSegment(sketch, "E157", {"start": v(-10.99, 625) * mm, "end": v(-10.99, 600) * mm});
            skLineSegment(sketch, "E158", {"start": v(13.55, 625) * mm, "end": v(13.55, 600) * mm});
            skLineSegment(sketch, "E159", {"start": v(33.8, 625) * mm, "end": v(33.8, 600) * mm});
            skSolve(sketch);
        }
        {
            var Q0;
            {var subQ9=sQuery(id+"F61.wireOp",EDGE,"E156");Q0=makeQuery(id+"F61.imprint","IMPRINT",FACE,{"disambiguationData":[TD([[makeQuery(id+"F61.imprint","IMPRINT",EDGE,{"derivedFrom":subQ9}),-1.0]])]});}
            var Q1;
            {var subQ0=sQuery(id+"F61.wireOp",EDGE,"E157");Q1=makeQuery(id+"F61.imprint","IMPRINT",FACE,{"disambiguationData":[TD([[makeQuery(id+"F61.imprint","IMPRINT",EDGE,{"derivedFrom":subQ0}),1.0]])]});}
            var Q2;
            {var subQ10=sQuery(id+"F61.wireOp",EDGE,"E159");Q2=makeQuery(id+"F61.imprint","IMPRINT",FACE,{"disambiguationData":[TD([[makeQuery(id+"F61.imprint","IMPRINT",EDGE,{"derivedFrom":subQ10}),1.0]])]});}
            extrude(context, id + "F62", {"entities" : qUnion([Q0, Q1, Q2]), "operationType" : NewBodyOperationType.ADD, "depth" : 2 * mm, "offsetDistance" : 25 * mm});
        }
        {
            var Q0;
            {var subQ4=sQuery(id+"F3.wireOp",EDGE,"E2.top");var subQ8=sQuery(id+"F3.wireOp",EDGE,"E2.right");var subQ23=makeQuery(id+"F4.opExtrude","SWEPT_FACE",FACE,{"disambiguationData":[OSD([subQ8])]});Q0=makeQuery(id+"F62.boolean.opBoolean","SPLIT",FACE,{"disambiguationData":[TD([makeQuery(id+"F62.opExtrude","SWEPT_FACE",FACE,{"disambiguationData":[OSD([sQuery(id+"F61.wireOp",EDGE,"E156")])]})])],"derivedFrom":makeQuery(id+"F57.boolean.opBoolean","MERGE",FACE,{"derivedFrom":[subQ23,makeQuery(id+"F57.opExtrude","SWEPT_FACE",FACE,{"disambiguationData":[OSD([subQ4,subQ8])]})]})});}
            var Q1;
            {var subQ4=sQuery(id+"F3.wireOp",EDGE,"E2.top");var subQ8=sQuery(id+"F3.wireOp",EDGE,"E2.right");var subQ22=sQuery(id+"F61.wireOp",EDGE,"E158");var subQ23=makeQuery(id+"F4.opExtrude","SWEPT_FACE",FACE,{"disambiguationData":[OSD([subQ8])]});Q1=makeQuery(id+"F62.boolean.opBoolean","SPLIT",FACE,{"disambiguationData":[TD([makeQuery(id+"F62.opExtrude","SWEPT_FACE",FACE,{"disambiguationData":[OSD([subQ22])]})])],"derivedFrom":makeQuery(id+"F57.boolean.opBoolean","MERGE",FACE,{"derivedFrom":[subQ23,makeQuery(id+"F57.opExtrude","SWEPT_FACE",FACE,{"disambiguationData":[OSD([subQ4,subQ8])]})]})});}
            extrude(context, id + "F63", {"entities" : qUnion([Q0, Q1]), "operationType" : NewBodyOperationType.ADD, "depth" : 1 * mm, "offsetDistance" : 25 * mm});
        }
        {
            var Q0;
            {var subQ0=sQuery(id+"F3.wireOp",EDGE,"E2.bottom");Q0=makeQuery(id+"F62.boolean.opBoolean","MERGE",FACE,{"derivedFrom":[makeQuery(id+"F59.boolean.opBoolean","MERGE",FACE,{"derivedFrom":[makeQuery(id+"F4.opExtrude","SWEPT_FACE",FACE,{"disambiguationData":[OSD([subQ0])]}),makeQuery(id+"F59.opExtrude","SWEPT_FACE",FACE,{"disambiguationData":[OSD([subQ0,sQuery(id+"F3.wireOp",EDGE,"E2.left")])]})]}),makeQuery(id+"F62.opExtrude","SWEPT_FACE",FACE,{"disambiguationData":[OSD([subQ0,sQuery(id+"F3.wireOp",EDGE,"E2.right")])]})]});}
            var sketch = newSketch(context, id + "F64", { "sketchPlane" : qUnion([Q0])});
            skLineSegment(sketch, "E160", {"start": v(-34.4, 625) * mm, "end": v(-34.4, 600) * mm});
            skLineSegment(sketch, "E161", {"start": v(-13.63, 625) * mm, "end": v(-13.63, 600) * mm});
            skLineSegment(sketch, "E162", {"start": v(7.3, 625) * mm, "end": v(7.3, 600) * mm});
            skLineSegment(sketch, "E163", {"start": v(34.4, 625) * mm, "end": v(34.4, 600) * mm});
            skSolve(sketch);
        }
        {
            var Q0;
            {var subQ11=sQuery(id+"F64.wireOp",EDGE,"E160");Q0=makeQuery(id+"F64.imprint","IMPRINT",FACE,{"disambiguationData":[TD([[makeQuery(id+"F64.imprint","IMPRINT",EDGE,{"derivedFrom":subQ11}),-1.0]])]});}
            var Q1;
            {var subQ0=sQuery(id+"F64.wireOp",EDGE,"E161");Q1=makeQuery(id+"F64.imprint","IMPRINT",FACE,{"disambiguationData":[TD([[makeQuery(id+"F64.imprint","IMPRINT",EDGE,{"derivedFrom":subQ0}),1.0]])]});}
            var Q2;
            {var subQ11=sQuery(id+"F64.wireOp",EDGE,"E163");Q2=makeQuery(id+"F64.imprint","IMPRINT",FACE,{"disambiguationData":[TD([[makeQuery(id+"F64.imprint","IMPRINT",EDGE,{"derivedFrom":subQ11}),1.0]])]});}
            extrude(context, id + "F65", {"entities" : qUnion([Q0, Q1, Q2]), "operationType" : NewBodyOperationType.ADD, "depth" : 1 * mm, "offsetDistance" : 25 * mm});
        }
        {
            var Q0;
            {var subQ2=sQuery(id+"F3.wireOp",EDGE,"E2.left");var subQ8=sQuery(id+"F3.wireOp",EDGE,"E2.right");var subQ9=sQuery(id+"F3.wireOp",EDGE,"E2.bottom");Q0=makeQuery(id+"F65.boolean.opBoolean","SPLIT",FACE,{"disambiguationData":[TD([makeQuery(id+"F65.opExtrude","SWEPT_FACE",FACE,{"disambiguationData":[OSD([sQuery(id+"F64.wireOp",EDGE,"E160")])]})])],"derivedFrom":makeQuery(id+"F62.boolean.opBoolean","MERGE",FACE,{"derivedFrom":[makeQuery(id+"F59.boolean.opBoolean","MERGE",FACE,{"derivedFrom":[makeQuery(id+"F4.opExtrude","SWEPT_FACE",FACE,{"disambiguationData":[OSD([subQ9])]}),makeQuery(id+"F59.opExtrude","SWEPT_FACE",FACE,{"disambiguationData":[OSD([subQ9,subQ2])]})]}),makeQuery(id+"F62.opExtrude","SWEPT_FACE",FACE,{"disambiguationData":[OSD([subQ9,subQ8])]})]})});}
            var Q1;
            {var subQ2=sQuery(id+"F3.wireOp",EDGE,"E2.left");var subQ8=sQuery(id+"F3.wireOp",EDGE,"E2.right");var subQ9=sQuery(id+"F3.wireOp",EDGE,"E2.bottom");Q1=makeQuery(id+"F65.boolean.opBoolean","SPLIT",FACE,{"disambiguationData":[TD([makeQuery(id+"F65.opExtrude","SWEPT_FACE",FACE,{"disambiguationData":[OSD([sQuery(id+"F64.wireOp",EDGE,"E162")])]})])],"derivedFrom":makeQuery(id+"F62.boolean.opBoolean","MERGE",FACE,{"derivedFrom":[makeQuery(id+"F59.boolean.opBoolean","MERGE",FACE,{"derivedFrom":[makeQuery(id+"F4.opExtrude","SWEPT_FACE",FACE,{"disambiguationData":[OSD([subQ9])]}),makeQuery(id+"F59.opExtrude","SWEPT_FACE",FACE,{"disambiguationData":[OSD([subQ9,subQ2])]})]}),makeQuery(id+"F62.opExtrude","SWEPT_FACE",FACE,{"disambiguationData":[OSD([subQ9,subQ8])]})]})});}
            extrude(context, id + "F66", {"entities" : qUnion([Q0, Q1]), "operationType" : NewBodyOperationType.ADD, "depth" : 2 * mm, "offsetDistance" : 25 * mm});
        }
        {
            var Q0;
            Q0=makeQuery(id+"F1.opExtrude","CAP_EDGE",EDGE,{"disambiguationData":[OSD([sQuery(id+"F0.wireOp",EDGE,"E0.left")])],"isStart":false});
            var Q1;
            Q1=makeQuery(id+"F1.opExtrude","CAP_EDGE",EDGE,{"disambiguationData":[OSD([sQuery(id+"F0.wireOp",EDGE,"E0.right")])],"isStart":false});
            chamfer(context, id + "F67", {"entities" : qUnion([Q0, Q1]), "width" : 20 * mm, "tangentPropagation" : true});
        }
        {
            var Q0;
            Q0=makeQuery(id+"F67.opChamfer","SPLIT",FACE,{"disambiguationData":[OD(0.0)],"derivedFrom":makeQuery(id+"F1.opExtrude","CAP_FACE",FACE,{"disambiguationData":[OSD([sQuery(id+"F0.wireOp",EDGE,"E0.bottom"),sQuery(id+"F0.wireOp",EDGE,"E0.top"),sQuery(id+"F0.wireOp",EDGE,"E0.left"),sQuery(id+"F0.wireOp",EDGE,"E0.right")])],"isStart":false})});
            var sketch = newSketch(context, id + "F68", { "sketchPlane" : qUnion([Q0])});
            skLineSegment(sketch, "E164.bottom", {"start": v(-53.68, -56.8) * mm, "end": v(-52.1, -56.8) * mm});
            skLineSegment(sketch, "E164.top", {"start": v(-53.68, -58) * mm, "end": v(-52.1, -58) * mm});
            skLineSegment(sketch, "E164.left", {"start": v(-53.68, -56.8) * mm, "end": v(-53.68, -58) * mm});
            skLineSegment(sketch, "E164.right", {"start": v(-52.1, -56.8) * mm, "end": v(-52.1, -58) * mm});
            skLineSegment(sketch, "E165.bottom", {"start": v(-53.68, -73.88) * mm, "end": v(-52.28, -73.88) * mm});
            skLineSegment(sketch, "E165.top", {"start": v(-53.68, -72.57) * mm, "end": v(-52.28, -72.57) * mm});
            skLineSegment(sketch, "E165.left", {"start": v(-53.68, -72.57) * mm, "end": v(-53.68, -73.88) * mm});
            skLineSegment(sketch, "E165.right", {"start": v(-52.28, -72.57) * mm, "end": v(-52.28, -73.88) * mm});
            skLineSegment(sketch, "E166.bottom", {"start": v(52.17, -57.3) * mm, "end": v(53.68, -57.3) * mm});
            skLineSegment(sketch, "E166.top", {"start": v(52.17, -58.55) * mm, "end": v(53.68, -58.55) * mm});
            skLineSegment(sketch, "E166.left", {"start": v(52.17, -57.3) * mm, "end": v(52.17, -58.55) * mm});
            skLineSegment(sketch, "E166.right", {"start": v(53.68, -57.3) * mm, "end": v(53.68, -58.55) * mm});
            skLineSegment(sketch, "E167.bottom", {"start": v(52.09, -72.65) * mm, "end": v(53.68, -72.65) * mm});
            skLineSegment(sketch, "E167.top", {"start": v(52.09, -73.88) * mm, "end": v(53.68, -73.88) * mm});
            skLineSegment(sketch, "E167.left", {"start": v(52.09, -72.65) * mm, "end": v(52.09, -73.88) * mm});
            skLineSegment(sketch, "E167.right", {"start": v(53.68, -72.65) * mm, "end": v(53.68, -73.88) * mm});
            skSolve(sketch);
        }
        {
            var Q0;
            Q0=makeQuery(id+"F68.imprint","IMPRINT",FACE,{"disambiguationData":[TD([[makeQuery(id+"F68.imprint","IMPRINT",EDGE,{"derivedFrom":sQuery(id+"F68.wireOp",EDGE,"E164.bottom")}),-1.0]])]});
            var Q1;
            Q1=makeQuery(id+"F68.imprint","IMPRINT",FACE,{"disambiguationData":[TD([[makeQuery(id+"F68.imprint","IMPRINT",EDGE,{"derivedFrom":sQuery(id+"F68.wireOp",EDGE,"E165.bottom")}),1.0]])]});
            var Q2;
            Q2=makeQuery(id+"F68.imprint","IMPRINT",FACE,{"disambiguationData":[TD([[makeQuery(id+"F68.imprint","IMPRINT",EDGE,{"derivedFrom":sQuery(id+"F68.wireOp",EDGE,"E167.bottom")}),-1.0]])]});
            var Q3;
            Q3=makeQuery(id+"F68.imprint","IMPRINT",FACE,{"disambiguationData":[TD([[makeQuery(id+"F68.imprint","IMPRINT",EDGE,{"derivedFrom":sQuery(id+"F68.wireOp",EDGE,"E166.bottom")}),-1.0]])]});
            extrude(context, id + "F69", {"entities" : qUnion([Q0, Q1, Q2, Q3]), "operationType" : NewBodyOperationType.ADD, "depth" : 8 * mm, "offsetDistance" : 25 * mm});
        }
        {
            var Q0;
            Q0=makeQuery(id+"F69.opExtrude","SWEPT_FACE",FACE,{"disambiguationData":[OSD([sQuery(id+"F68.wireOp",EDGE,"E165.bottom")])]});
            var sketch = newSketch(context, id + "F70", { "sketchPlane" : qUnion([Q0])});
            skLineSegment(sketch, "E168.bottom", {"start": v(-53.68, 608) * mm, "end": v(53.8, 608) * mm});
            skLineSegment(sketch, "E168.top", {"start": v(-53.68, 600) * mm, "end": v(53.8, 600) * mm});
            skLineSegment(sketch, "E168.left", {"start": v(-53.68, 608) * mm, "end": v(-53.68, 600) * mm});
            skLineSegment(sketch, "E168.right", {"start": v(53.8, 608) * mm, "end": v(53.8, 600) * mm});
            skSolve(sketch);
        }
        {
            var Q0;
            {var subQ3=sQuery(id+"F70.wireOp",EDGE,"E168.right");Q0=makeQuery(id+"F70.imprint","IMPRINT",FACE,{"disambiguationData":[TD([[makeQuery(id+"F70.imprint","IMPRINT",EDGE,{"derivedFrom":subQ3}),-1.0]])]});}
            extrude(context, id + "F71", {"entities" : qUnion([Q0]), "depth" : 0.2 * mm, "offsetDistance" : 25 * mm});
        }
        {
            var Q0;
            Q0=makeQuery(id+"F69.opExtrude","SWEPT_FACE",FACE,{"disambiguationData":[OSD([sQuery(id+"F68.wireOp",EDGE,"E165.left")])]});
            var sketch = newSketch(context, id + "F72", { "sketchPlane" : qUnion([Q0])});
            skLineSegment(sketch, "E169.bottom", {"start": v(73.88, 608) * mm, "end": v(55.34, 608) * mm});
            skLineSegment(sketch, "E169.top", {"start": v(73.88, 600.1) * mm, "end": v(55.34, 600.1) * mm});
            skLineSegment(sketch, "E169.left", {"start": v(73.88, 608) * mm, "end": v(73.88, 600.1) * mm});
            skLineSegment(sketch, "E169.right", {"start": v(55.34, 608) * mm, "end": v(55.34, 600.1) * mm});
            skSolve(sketch);
        }
        {
            var Q0;
            {var subQ3=sQuery(id+"F72.wireOp",EDGE,"E169.right");Q0=makeQuery(id+"F72.imprint","IMPRINT",FACE,{"disambiguationData":[TD([[makeQuery(id+"F72.imprint","IMPRINT",EDGE,{"derivedFrom":subQ3}),1.0]])]});}
            extrude(context, id + "F73", {"entities" : qUnion([Q0]), "depth" : 0.2 * mm, "offsetDistance" : 25 * mm});
        }
        {
            var Q0;
            Q0=makeQuery(id+"F69.opExtrude","SWEPT_FACE",FACE,{"disambiguationData":[OSD([sQuery(id+"F68.wireOp",EDGE,"E167.right")])]});
            var sketch = newSketch(context, id + "F74", { "sketchPlane" : qUnion([Q0])});
            skLineSegment(sketch, "E170.bottom", {"start": v(-73.88, 608) * mm, "end": v(-56.19, 608) * mm});
            skLineSegment(sketch, "E170.top", {"start": v(-73.88, 599.92) * mm, "end": v(-56.19, 599.92) * mm});
            skLineSegment(sketch, "E170.left", {"start": v(-73.88, 608) * mm, "end": v(-73.88, 599.92) * mm});
            skLineSegment(sketch, "E170.right", {"start": v(-56.19, 608) * mm, "end": v(-56.19, 599.92) * mm});
            skSolve(sketch);
        }
        {
            var Q0;
            {var subQ3=sQuery(id+"F74.wireOp",EDGE,"E170.top");Q0=makeQuery(id+"F74.imprint","IMPRINT",FACE,{"disambiguationData":[TD([[makeQuery(id+"F74.imprint","IMPRINT",EDGE,{"derivedFrom":subQ3}),1.0]])]});}
            extrude(context, id + "F75", {"entities" : qUnion([Q0]), "depth" : 0.2 * mm, "offsetDistance" : 25 * mm});
        }
    });
